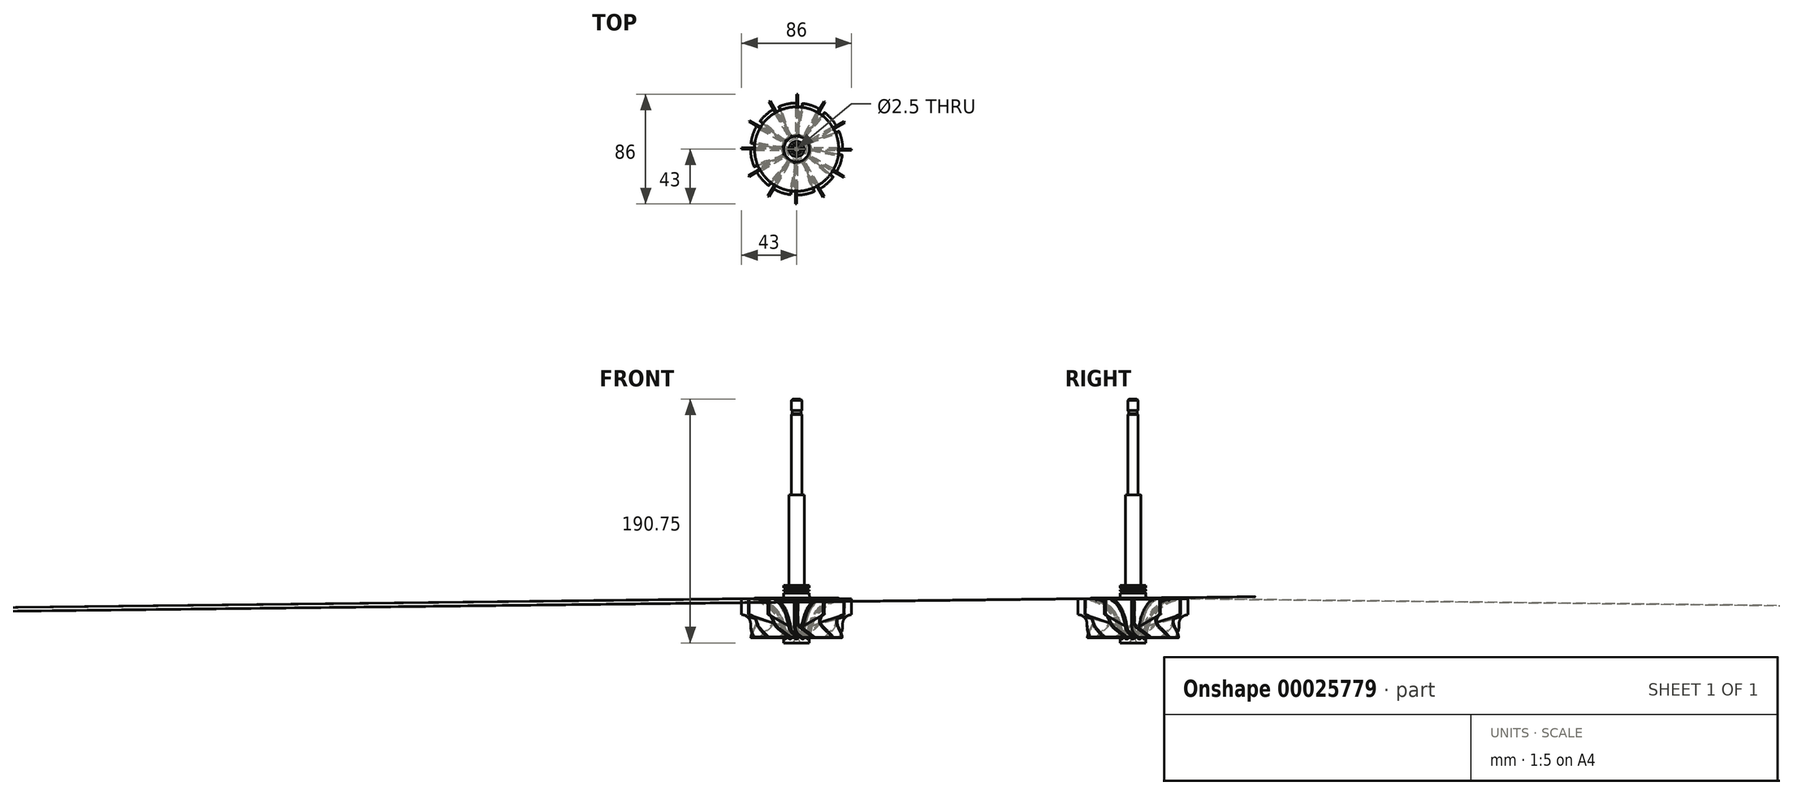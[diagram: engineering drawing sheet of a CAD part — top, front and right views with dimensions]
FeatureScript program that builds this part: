
annotation { "Feature Type Name" : "Feature", "Feature Type Description" : "" }
export const myFeature = defineFeature(function(context is Context, id is Id, definition is map)
    precondition{}
    {
        {
            var Q0;
            Q0=qCreatedBy(makeId("Front.planeOp"),FACE);
            var sketch = newSketch(context, id + "F0", { "sketchPlane" : qUnion([Q0])});
            skLineSegment(sketch, "E0", {"start": v(-6, -75) * mm, "end": v(-6, -145.75) * mm});
            skLineSegment(sketch, "E1", {"start": v(-43, -155.75) * mm, "end": v(-43, -168.75) * mm, "construction": true});
            skLineSegment(sketch, "E2", {"start": v(-43, -155.75) * mm, "end": v(-32.5, -155.75) * mm, "construction": true});
            skLineSegment(sketch, "E3", {"start": v(-10, -145.75) * mm, "end": v(-6, -145.75) * mm});
            skLineSegment(sketch, "E4", {"start": v(-6, -75) * mm, "end": v(-4, -75) * mm});
            skLineSegment(sketch, "E5", {"start": v(-4, 0) * mm, "end": v(0, 0) * mm});
            skLineSegment(sketch, "E6", {"start": v(0, 0) * mm, "end": v(0, -190.75) * mm});
            skLineSegment(sketch, "E7", {"start": v(-4, 0) * mm, "end": v(-4, -9) * mm});
            skLineSegment(sketch, "E8", {"start": v(-3.4, -9) * mm, "end": v(-3.4, -11.4) * mm});
            skLineSegment(sketch, "E9", {"start": v(-3.4, -11.4) * mm, "end": v(-4, -12) * mm});
            skLineSegment(sketch, "E10", {"start": v(-4, -12) * mm, "end": v(-4, -75) * mm});
            skLineSegment(sketch, "E11", {"start": v(-4, -9) * mm, "end": v(-3.4, -9) * mm});
            skLineSegment(sketch, "E12", {"start": v(-10, -145.75) * mm, "end": v(-10, -147.75) * mm});
            skLineSegment(sketch, "E13", {"start": v(-36, -175.75) * mm, "end": v(-36, -186.75) * mm, "construction": true});
            skLineSegment(sketch, "E14", {"start": v(-43, -168.75) * mm, "end": v(-43, -168.75) * mm});
            skLineSegment(sketch, "E15", {"start": v(-36, -186.75) * mm, "end": v(-10, -186.75) * mm, "construction": true});
            skLineSegment(sketch, "E16", {"start": v(-10, -186.75) * mm, "end": v(-10, -190.75) * mm});
            skLineSegment(sketch, "E17", {"start": v(-10, -190.75) * mm, "end": v(0, -190.75) * mm});
            skPoint(sketch, "E18.visualSharp", {"position": v(-36, -168.75) * mm});
            skArc(sketch, "E18.filletArc", {"start": v(-36, -175.75) * mm, "mid": v(-38.05, -170.8) * mm, "end": v(-43, -168.75) * mm, "construction": true});
            skLineSegment(sketch, "E19", {"start": v(-32.5, -155.75) * mm, "end": v(-32.5, -156.75) * mm, "construction": true});
            skArc(sketch, "E20", {"start": v(-32.5, -155.75) * mm, "mid": v(-33, -156.25) * mm, "end": v(-32.5, -156.75) * mm});
            skArc(sketch, "E21", {"start": v(-10, -186.75) * mm, "mid": v(-16.25, -168) * mm, "end": v(-32.5, -156.75) * mm});
            skLineSegment(sketch, "E22", {"start": v(-32.5, -155.75) * mm, "end": v(-10, -155.75) * mm});
            skLineSegment(sketch, "E23", {"start": v(-2.9, -190.75) * mm, "end": v(-1.5, -188.32) * mm});
            skLineSegment(sketch, "E24", {"start": v(-1.5, -188.32) * mm, "end": v(-1.5, -186.8) * mm});
            skLineSegment(sketch, "E25", {"start": v(-1.5, -186.8) * mm, "end": v(0, -185.9) * mm});
            skLineSegment(sketch, "E26", {"start": v(-8, -147.75) * mm, "end": v(-8, -149.25) * mm});
            skLineSegment(sketch, "E27", {"start": v(-8, -147.75) * mm, "end": v(-10, -147.75) * mm});
            skLineSegment(sketch, "E28", {"start": v(-8, -149.25) * mm, "end": v(-10, -149.25) * mm});
            skLineSegment(sketch, "E29", {"start": v(-8, -150.25) * mm, "end": v(-10, -150.25) * mm});
            skLineSegment(sketch, "E30", {"start": v(-8, -151.75) * mm, "end": v(-10, -151.75) * mm});
            skPoint(sketch, "E31.orphan", {"position": v(-8, -155.75) * mm});
            skLineSegment(sketch, "E32.trimOffspring", {"start": v(-8, -150.25) * mm, "end": v(-8, -151.75) * mm});
            skLineSegment(sketch, "E33.trimOffspring", {"start": v(-10, -149.25) * mm, "end": v(-10, -150.25) * mm});
            skLineSegment(sketch, "E34.trimOffspring", {"start": v(-10, -151.75) * mm, "end": v(-10, -155.75) * mm});
            skSolve(sketch);
        }
        {
            var Q0;
            Q0 = qSketchRegion(id + "F0", true);
            var Q1;
            Q1=sQuery(id+"F0.wireOp",EDGE,"E6");
            revolve(context, id + "F1", {"entities" : qUnion([Q0]), "axis" : qUnion([Q1]), "revolveType" : RevolveType.FULL});
        }
        {
            var Q0;
            Q0=makeQuery(id+"F1.opRevolve","SWEPT_EDGE",EDGE,{"disambiguationData":[OSD([sQuery(id+"F0.wireOp",EDGE,"E22"),sQuery(id+"F0.wireOp",EDGE,"E34.trimOffspring")])]});
            fillet(context, id + "F2", {"entities" : qUnion([Q0]), "radius" : 2 * mm, "tangentPropagation" : true, "allowEdgeOverflow" : false});
        }
        {
            var Q0;
            Q0=makeQuery(id+"F1.opRevolve","SWEPT_EDGE",EDGE,{"disambiguationData":[OSD([sQuery(id+"F0.wireOp",EDGE,"E5"),sQuery(id+"F0.wireOp",EDGE,"E7")])]});
            chamfer(context, id + "F3", {"entities" : qUnion([Q0]), "width" : 1 * mm, "tangentPropagation" : true});
        }
        {
            var Q0;
            Q0=qCreatedBy(makeId("Front.planeOp"),FACE);
            var sketch = newSketch(context, id + "F4", { "sketchPlane" : qUnion([Q0])});
            skLineSegment(sketch, "E35", {"start": v(0, -1.47) * mm, "end": v(0, -247.78) * mm, "construction": true});
            skLineSegment(sketch, "E36", {"start": v(0, -155.75) * mm, "end": v(0, -181.26) * mm});
            skPoint(sketch, "E37.orphan", {"position": v(0.08, -187.45) * mm});
            skLineSegment(sketch, "E38", {"start": v(3, -186.75) * mm, "end": v(1.76, -185.5) * mm});
            skPoint(sketch, "E39.visualSharp", {"position": v(0, -183.75) * mm});
            skArc(sketch, "E39.filletArc", {"start": v(0, -181.26) * mm, "mid": v(0.46, -183.56) * mm, "end": v(1.76, -185.5) * mm});
            skLineSegment(sketch, "E40.0", {"start": v(1.59, -186.75) * mm, "end": v(1.05, -186.21) * mm});
            skArc(sketch, "E40.1", {"start": v(-1, -181.26) * mm, "mid": v(-0.47, -183.94) * mm, "end": v(1.05, -186.21) * mm});
            skLineSegment(sketch, "E40.2", {"start": v(-1, -155.75) * mm, "end": v(-1, -181.26) * mm});
            skLineSegment(sketch, "E41", {"start": v(-1, -155.75) * mm, "end": v(0, -155.75) * mm});
            skLineSegment(sketch, "E42", {"start": v(3, -186.75) * mm, "end": v(1.59, -186.75) * mm});
            skSolve(sketch);
        }
        {
            var Q0;
            Q0=qCreatedBy(makeId("Front.planeOp"),FACE);
            cPlane(context, id + "F5", {"entities" : qUnion([Q0]), "cplaneType" : CPlaneType.OFFSET, "offset" : 43 * mm, "width" : 150 * mm, "height" : 150 * mm});
        }
        {
            var Q0;
            Q0=qCreatedBy(id+"F5.planeOp",FACE);
            var sketch = newSketch(context, id + "F6", { "sketchPlane" : qUnion([Q0])});
            skLineSegment(sketch, "E43", {"start": v(0, -186.75) * mm, "end": v(18, -186.75) * mm, "construction": true});
            skLineSegment(sketch, "E44", {"start": v(0, -156.25) * mm, "end": v(0, -168.75) * mm});
            skLineSegment(sketch, "E45", {"start": v(18, -186.75) * mm, "end": v(4.42, -177.24) * mm});
            skArc(sketch, "E46", {"start": v(0, -168.75) * mm, "mid": v(1.17, -173.54) * mm, "end": v(4.42, -177.24) * mm});
            skLineSegment(sketch, "E47.0", {"start": v(16.26, -186.75) * mm, "end": v(3.85, -178.06) * mm});
            skArc(sketch, "E47.1", {"start": v(-1, -168.75) * mm, "mid": v(0.28, -174) * mm, "end": v(3.85, -178.06) * mm});
            skLineSegment(sketch, "E47.2", {"start": v(-1, -156.25) * mm, "end": v(-1, -168.75) * mm});
            skLineSegment(sketch, "E48", {"start": v(18, -186.75) * mm, "end": v(16.26, -186.75) * mm});
            skPoint(sketch, "E49.orphan", {"position": v(-14.5, -155.75) * mm});
            skPoint(sketch, "E50.orphan", {"position": v(14.5, -155.75) * mm});
            skLineSegment(sketch, "E51", {"start": v(0, -156.25) * mm, "end": v(-1, -156.25) * mm});
            skPoint(sketch, "E52.orphan", {"position": v(0, -155.75) * mm});
            skSolve(sketch);
        }
        {
            var Q1;
            Q1 = qSketchRegion(id + "F4", true);
            var Q2;
            Q2 = qSketchRegion(id + "F6", true);
            loft(context, id + "F7", {"operationType" : NewBodyOperationType.ADD, "sheetProfilesArray" : [{ "sheetProfileEntities" : qUnion([Q1]) }, { "sheetProfileEntities" : qUnion([Q2]) }]});
        }
        {
            var Q0;
            Q0=makeQuery(id+"F7.opLoft","SWEPT_FACE",FACE,{"disambiguationData":[OSD([sQuery(id+"F4.wireOp",EDGE,"E40.0"),sQuery(id+"F4.wireOp",EDGE,"E40.1"),sQuery(id+"F4.wireOp",EDGE,"E40.2"),sQuery(id+"F6.wireOp",EDGE,"E47.0"),sQuery(id+"F6.wireOp",EDGE,"E47.1"),sQuery(id+"F6.wireOp",EDGE,"E47.2")])]});
            var Q1;
            Q1=makeQuery(id+"F7.opLoft","SWEPT_FACE",FACE,{"disambiguationData":[OSD([sQuery(id+"F4.wireOp",EDGE,"E38"),sQuery(id+"F4.wireOp",EDGE,"E40.0"),sQuery(id+"F4.wireOp",EDGE,"E42"),sQuery(id+"F6.wireOp",EDGE,"E45"),sQuery(id+"F6.wireOp",EDGE,"E47.0"),sQuery(id+"F6.wireOp",EDGE,"E48")])]});
            var Q2;
            Q2=makeQuery(id+"F7.opLoft","CAP_FACE",FACE,{"disambiguationData":[OSD([makeQuery(id+"F6.imprint","IMPRINT",FACE,{"disambiguationData":[TD([[makeQuery(id+"F6.imprint","IMPRINT",EDGE,{"derivedFrom":sQuery(id+"F6.wireOp",EDGE,"E44")}),-1.0]])]})])],"isStart":true});
            var Q3;
            Q3=makeQuery(id+"F7.opLoft","SWEPT_FACE",FACE,{"disambiguationData":[OSD([sQuery(id+"F4.wireOp",EDGE,"E38"),sQuery(id+"F4.wireOp",EDGE,"E39.filletArc"),sQuery(id+"F4.wireOp",EDGE,"E42"),sQuery(id+"F6.wireOp",EDGE,"E45"),sQuery(id+"F6.wireOp",EDGE,"E46"),sQuery(id+"F6.wireOp",EDGE,"E48")])]});
            var Q4;
            Q4=makeQuery(id+"F7.opLoft","SWEPT_FACE",FACE,{"disambiguationData":[OSD([sQuery(id+"F4.wireOp",EDGE,"E36"),sQuery(id+"F4.wireOp",EDGE,"E39.filletArc"),sQuery(id+"F4.wireOp",EDGE,"E41"),sQuery(id+"F6.wireOp",EDGE,"E44"),sQuery(id+"F6.wireOp",EDGE,"E46"),sQuery(id+"F6.wireOp",EDGE,"E51")])]});
            var Q5;
            Q5=makeQuery(id+"F7.opLoft","SWEPT_FACE",FACE,{"disambiguationData":[OSD([sQuery(id+"F4.wireOp",EDGE,"E40.1"),sQuery(id+"F4.wireOp",EDGE,"E40.2"),sQuery(id+"F4.wireOp",EDGE,"E41"),sQuery(id+"F6.wireOp",EDGE,"E47.1"),sQuery(id+"F6.wireOp",EDGE,"E47.2"),sQuery(id+"F6.wireOp",EDGE,"E51")])]});
            var Q6;
            Q6=makeQuery(id+"F7.opLoft","SWEPT_FACE",FACE,{"disambiguationData":[OSD([sQuery(id+"F4.wireOp",EDGE,"E36"),sQuery(id+"F4.wireOp",EDGE,"E40.2"),sQuery(id+"F4.wireOp",EDGE,"E41"),sQuery(id+"F6.wireOp",EDGE,"E44"),sQuery(id+"F6.wireOp",EDGE,"E47.2"),sQuery(id+"F6.wireOp",EDGE,"E51")])]});
            var Q7;
            Q7=makeQuery(id+"F1.opRevolve","SWEPT_FACE",FACE,{"disambiguationData":[OSD([sQuery(id+"F0.wireOp",EDGE,"E0")])]});
            circularPattern(context, id + "F8", {"faces" : qUnion([Q0, Q1, Q2, Q3, Q4, Q5, Q6]), "axis" : qUnion([Q7]), "angle" : 30 * degree, "instanceCount" : 12, "patternType" : PatternType.FACE});
        }
        {
            var Q0;
            Q0=qCreatedBy(makeId("Front.planeOp"),FACE);
            var sketch = newSketch(context, id + "F9", { "sketchPlane" : qUnion([Q0])});
            skLineSegment(sketch, "E53.0", {"start": v(43, -156.25) * mm, "end": v(43, -168.75) * mm});
            skLineSegment(sketch, "E54", {"start": v(43, -168.75) * mm, "end": v(43, -168.75) * mm});
            skLineSegment(sketch, "E55", {"start": v(36, -175.75) * mm, "end": v(36, -190.75) * mm});
            skLineSegment(sketch, "E56", {"start": v(0, 28.12) * mm, "end": v(0, -228.95) * mm, "construction": true});
            skLineSegment(sketch, "E57", {"start": v(43, -168.75) * mm, "end": v(50.1, -168.75) * mm});
            skLineSegment(sketch, "E58.0", {"start": v(-10, -190.75) * mm, "end": v(10, -190.75) * mm});
            skLineSegment(sketch, "E59", {"start": v(36, -190.75) * mm, "end": v(50.1, -190.75) * mm});
            skLineSegment(sketch, "E60", {"start": v(50.1, -168.75) * mm, "end": v(50.1, -190.75) * mm});
            skPoint(sketch, "E61.visualSharp", {"position": v(36, -168.75) * mm});
            skArc(sketch, "E61.filletArc", {"start": v(43, -168.75) * mm, "mid": v(38.05, -170.8) * mm, "end": v(36, -175.75) * mm});
            skSolve(sketch);
        }
        {
            var Q0;
            Q0 = qSketchRegion(id + "F9", true);
            var Q1;
            Q1=sQuery(id+"F9.wireOp",EDGE,"E56");
            revolve(context, id + "F10", {"operationType" : NewBodyOperationType.REMOVE, "entities" : qUnion([Q0]), "axis" : qUnion([Q1]), "revolveType" : RevolveType.FULL, "oppositeDirection" : true});
        }
        {
            var Q0;
            Q0=qCreatedBy(makeId("Front.planeOp"),FACE);
            var sketch = newSketch(context, id + "F11", { "sketchPlane" : qUnion([Q0])});
            skLineSegment(sketch, "E62", {"start": v(0, 44.53) * mm, "end": v(0, -214.06) * mm, "construction": true});
            skLineSegment(sketch, "E63.0", {"start": v(0, -190.75) * mm, "end": v(2.98, -190.75) * mm});
            skLineSegment(sketch, "E64", {"start": v(0, -190.75) * mm, "end": v(0, -185) * mm});
            skLineSegment(sketch, "E65", {"start": v(0, -185) * mm, "end": v(1.25, -185.75) * mm});
            skLineSegment(sketch, "E66", {"start": v(1.25, -185.75) * mm, "end": v(1.25, -187.75) * mm});
            skLineSegment(sketch, "E67", {"start": v(1.25, -187.75) * mm, "end": v(2.98, -190.75) * mm});
            skPoint(sketch, "E68.orphan", {"position": v(10, -190.75) * mm});
            skPoint(sketch, "E69.orphan", {"position": v(-10, -190.75) * mm});
            skSolve(sketch);
        }
        {
            var Q0;
            Q0 = qSketchRegion(id + "F11", true);
            var Q1;
            Q1=sQuery(id+"F11.wireOp",EDGE,"E62");
            revolve(context, id + "F12", {"operationType" : NewBodyOperationType.REMOVE, "entities" : qUnion([Q0]), "axis" : qUnion([Q1]), "revolveType" : RevolveType.FULL, "oppositeDirection" : true});
        }
        {
            var Q0;
            Q0=makeQuery(id+"F8.opPattern","COPY",EDGE,{"derivedFrom":makeQuery(id+"F7.opLoft","SWEPT_EDGE",EDGE,{"disambiguationData":[OSD([sQuery(id+"F4.wireOp",EDGE,"E38"),sQuery(id+"F4.wireOp",EDGE,"E42"),sQuery(id+"F6.wireOp",EDGE,"E45"),sQuery(id+"F6.wireOp",EDGE,"E48")])]}),"instanceName":"4"});
            var Q1;
            Q1=makeQuery(id+"F8.opPattern","COPY",EDGE,{"derivedFrom":makeQuery(id+"F7.opLoft","SWEPT_EDGE",EDGE,{"disambiguationData":[OSD([sQuery(id+"F4.wireOp",EDGE,"E38"),sQuery(id+"F4.wireOp",EDGE,"E42"),sQuery(id+"F6.wireOp",EDGE,"E45"),sQuery(id+"F6.wireOp",EDGE,"E48")])]}),"instanceName":"3"});
            var Q2;
            Q2=makeQuery(id+"F8.opPattern","COPY",EDGE,{"derivedFrom":makeQuery(id+"F7.opLoft","SWEPT_EDGE",EDGE,{"disambiguationData":[OSD([sQuery(id+"F4.wireOp",EDGE,"E38"),sQuery(id+"F4.wireOp",EDGE,"E42"),sQuery(id+"F6.wireOp",EDGE,"E45"),sQuery(id+"F6.wireOp",EDGE,"E48")])]}),"instanceName":"2"});
            var Q3;
            Q3=makeQuery(id+"F8.opPattern","COPY",EDGE,{"derivedFrom":makeQuery(id+"F7.opLoft","SWEPT_EDGE",EDGE,{"disambiguationData":[OSD([sQuery(id+"F4.wireOp",EDGE,"E38"),sQuery(id+"F4.wireOp",EDGE,"E42"),sQuery(id+"F6.wireOp",EDGE,"E45"),sQuery(id+"F6.wireOp",EDGE,"E48")])]}),"instanceName":"1"});
            var Q4;
            Q4=makeQuery(id+"F7.opLoft","SWEPT_EDGE",EDGE,{"disambiguationData":[OSD([sQuery(id+"F4.wireOp",EDGE,"E38"),sQuery(id+"F4.wireOp",EDGE,"E42"),sQuery(id+"F6.wireOp",EDGE,"E45"),sQuery(id+"F6.wireOp",EDGE,"E48")])]});
            var Q5;
            Q5=makeQuery(id+"F8.opPattern","COPY",EDGE,{"derivedFrom":makeQuery(id+"F7.opLoft","SWEPT_EDGE",EDGE,{"disambiguationData":[OSD([sQuery(id+"F4.wireOp",EDGE,"E38"),sQuery(id+"F4.wireOp",EDGE,"E42"),sQuery(id+"F6.wireOp",EDGE,"E45"),sQuery(id+"F6.wireOp",EDGE,"E48")])]}),"instanceName":"11"});
            var Q6;
            Q6=makeQuery(id+"F8.opPattern","COPY",EDGE,{"derivedFrom":makeQuery(id+"F7.opLoft","SWEPT_EDGE",EDGE,{"disambiguationData":[OSD([sQuery(id+"F4.wireOp",EDGE,"E38"),sQuery(id+"F4.wireOp",EDGE,"E42"),sQuery(id+"F6.wireOp",EDGE,"E45"),sQuery(id+"F6.wireOp",EDGE,"E48")])]}),"instanceName":"10"});
            var Q7;
            Q7=makeQuery(id+"F8.opPattern","COPY",EDGE,{"derivedFrom":makeQuery(id+"F7.opLoft","SWEPT_EDGE",EDGE,{"disambiguationData":[OSD([sQuery(id+"F4.wireOp",EDGE,"E38"),sQuery(id+"F4.wireOp",EDGE,"E42"),sQuery(id+"F6.wireOp",EDGE,"E45"),sQuery(id+"F6.wireOp",EDGE,"E48")])]}),"instanceName":"9"});
            var Q8;
            Q8=makeQuery(id+"F8.opPattern","COPY",EDGE,{"derivedFrom":makeQuery(id+"F7.opLoft","SWEPT_EDGE",EDGE,{"disambiguationData":[OSD([sQuery(id+"F4.wireOp",EDGE,"E38"),sQuery(id+"F4.wireOp",EDGE,"E42"),sQuery(id+"F6.wireOp",EDGE,"E45"),sQuery(id+"F6.wireOp",EDGE,"E48")])]}),"instanceName":"8"});
            var Q9;
            Q9=makeQuery(id+"F8.opPattern","COPY",EDGE,{"derivedFrom":makeQuery(id+"F7.opLoft","SWEPT_EDGE",EDGE,{"disambiguationData":[OSD([sQuery(id+"F4.wireOp",EDGE,"E38"),sQuery(id+"F4.wireOp",EDGE,"E42"),sQuery(id+"F6.wireOp",EDGE,"E45"),sQuery(id+"F6.wireOp",EDGE,"E48")])]}),"instanceName":"7"});
            var Q10;
            Q10=makeQuery(id+"F8.opPattern","COPY",EDGE,{"derivedFrom":makeQuery(id+"F7.opLoft","SWEPT_EDGE",EDGE,{"disambiguationData":[OSD([sQuery(id+"F4.wireOp",EDGE,"E38"),sQuery(id+"F4.wireOp",EDGE,"E42"),sQuery(id+"F6.wireOp",EDGE,"E45"),sQuery(id+"F6.wireOp",EDGE,"E48")])]}),"instanceName":"6"});
            var Q11;
            Q11=makeQuery(id+"F8.opPattern","COPY",EDGE,{"derivedFrom":makeQuery(id+"F7.opLoft","SWEPT_EDGE",EDGE,{"disambiguationData":[OSD([sQuery(id+"F4.wireOp",EDGE,"E38"),sQuery(id+"F4.wireOp",EDGE,"E42"),sQuery(id+"F6.wireOp",EDGE,"E45"),sQuery(id+"F6.wireOp",EDGE,"E48")])]}),"instanceName":"5"});
            fillet(context, id + "F13", {"entities" : qUnion([Q0, Q1, Q2, Q3, Q4, Q5, Q6, Q7, Q8, Q9, Q10, Q11]), "radius" : .3 * mm, "tangentPropagation" : true, "allowEdgeOverflow" : false});
        }
        {
            var Q0;
            Q0=makeQuery(id+"F8.opPattern","COPY",EDGE,{"derivedFrom":makeQuery(id+"F7.opLoft","SWEPT_EDGE",EDGE,{"disambiguationData":[OSD([sQuery(id+"F4.wireOp",EDGE,"E40.0"),sQuery(id+"F4.wireOp",EDGE,"E42"),sQuery(id+"F6.wireOp",EDGE,"E47.0"),sQuery(id+"F6.wireOp",EDGE,"E48")])]}),"instanceName":"5"});
            var Q1;
            Q1=makeQuery(id+"F8.opPattern","COPY",EDGE,{"derivedFrom":makeQuery(id+"F7.opLoft","SWEPT_EDGE",EDGE,{"disambiguationData":[OSD([sQuery(id+"F4.wireOp",EDGE,"E40.0"),sQuery(id+"F4.wireOp",EDGE,"E42"),sQuery(id+"F6.wireOp",EDGE,"E47.0"),sQuery(id+"F6.wireOp",EDGE,"E48")])]}),"instanceName":"4"});
            var Q2;
            Q2=makeQuery(id+"F8.opPattern","COPY",EDGE,{"derivedFrom":makeQuery(id+"F7.opLoft","SWEPT_EDGE",EDGE,{"disambiguationData":[OSD([sQuery(id+"F4.wireOp",EDGE,"E40.0"),sQuery(id+"F4.wireOp",EDGE,"E42"),sQuery(id+"F6.wireOp",EDGE,"E47.0"),sQuery(id+"F6.wireOp",EDGE,"E48")])]}),"instanceName":"3"});
            var Q3;
            Q3=makeQuery(id+"F8.opPattern","COPY",EDGE,{"derivedFrom":makeQuery(id+"F7.opLoft","SWEPT_EDGE",EDGE,{"disambiguationData":[OSD([sQuery(id+"F4.wireOp",EDGE,"E40.0"),sQuery(id+"F4.wireOp",EDGE,"E42"),sQuery(id+"F6.wireOp",EDGE,"E47.0"),sQuery(id+"F6.wireOp",EDGE,"E48")])]}),"instanceName":"2"});
            var Q4;
            Q4=makeQuery(id+"F8.opPattern","COPY",EDGE,{"derivedFrom":makeQuery(id+"F7.opLoft","SWEPT_EDGE",EDGE,{"disambiguationData":[OSD([sQuery(id+"F4.wireOp",EDGE,"E40.0"),sQuery(id+"F4.wireOp",EDGE,"E42"),sQuery(id+"F6.wireOp",EDGE,"E47.0"),sQuery(id+"F6.wireOp",EDGE,"E48")])]}),"instanceName":"1"});
            var Q5;
            Q5=makeQuery(id+"F7.opLoft","SWEPT_EDGE",EDGE,{"disambiguationData":[OSD([sQuery(id+"F4.wireOp",EDGE,"E40.0"),sQuery(id+"F4.wireOp",EDGE,"E42"),sQuery(id+"F6.wireOp",EDGE,"E47.0"),sQuery(id+"F6.wireOp",EDGE,"E48")])]});
            var Q6;
            Q6=makeQuery(id+"F8.opPattern","COPY",EDGE,{"derivedFrom":makeQuery(id+"F7.opLoft","SWEPT_EDGE",EDGE,{"disambiguationData":[OSD([sQuery(id+"F4.wireOp",EDGE,"E40.0"),sQuery(id+"F4.wireOp",EDGE,"E42"),sQuery(id+"F6.wireOp",EDGE,"E47.0"),sQuery(id+"F6.wireOp",EDGE,"E48")])]}),"instanceName":"11"});
            var Q7;
            Q7=makeQuery(id+"F8.opPattern","COPY",EDGE,{"derivedFrom":makeQuery(id+"F7.opLoft","SWEPT_EDGE",EDGE,{"disambiguationData":[OSD([sQuery(id+"F4.wireOp",EDGE,"E40.0"),sQuery(id+"F4.wireOp",EDGE,"E42"),sQuery(id+"F6.wireOp",EDGE,"E47.0"),sQuery(id+"F6.wireOp",EDGE,"E48")])]}),"instanceName":"10"});
            var Q8;
            Q8=makeQuery(id+"F8.opPattern","COPY",EDGE,{"derivedFrom":makeQuery(id+"F7.opLoft","SWEPT_EDGE",EDGE,{"disambiguationData":[OSD([sQuery(id+"F4.wireOp",EDGE,"E40.0"),sQuery(id+"F4.wireOp",EDGE,"E42"),sQuery(id+"F6.wireOp",EDGE,"E47.0"),sQuery(id+"F6.wireOp",EDGE,"E48")])]}),"instanceName":"9"});
            var Q9;
            Q9=makeQuery(id+"F8.opPattern","COPY",EDGE,{"derivedFrom":makeQuery(id+"F7.opLoft","SWEPT_EDGE",EDGE,{"disambiguationData":[OSD([sQuery(id+"F4.wireOp",EDGE,"E40.0"),sQuery(id+"F4.wireOp",EDGE,"E42"),sQuery(id+"F6.wireOp",EDGE,"E47.0"),sQuery(id+"F6.wireOp",EDGE,"E48")])]}),"instanceName":"8"});
            var Q10;
            Q10=makeQuery(id+"F8.opPattern","COPY",EDGE,{"derivedFrom":makeQuery(id+"F7.opLoft","SWEPT_EDGE",EDGE,{"disambiguationData":[OSD([sQuery(id+"F4.wireOp",EDGE,"E40.0"),sQuery(id+"F4.wireOp",EDGE,"E42"),sQuery(id+"F6.wireOp",EDGE,"E47.0"),sQuery(id+"F6.wireOp",EDGE,"E48")])]}),"instanceName":"7"});
            var Q11;
            Q11=makeQuery(id+"F8.opPattern","COPY",EDGE,{"derivedFrom":makeQuery(id+"F7.opLoft","SWEPT_EDGE",EDGE,{"disambiguationData":[OSD([sQuery(id+"F4.wireOp",EDGE,"E40.0"),sQuery(id+"F4.wireOp",EDGE,"E42"),sQuery(id+"F6.wireOp",EDGE,"E47.0"),sQuery(id+"F6.wireOp",EDGE,"E48")])]}),"instanceName":"6"});
            fillet(context, id + "F14", {"entities" : qUnion([Q0, Q1, Q2, Q3, Q4, Q5, Q6, Q7, Q8, Q9, Q10, Q11]), "radius" : 1.5 * mm, "tangentPropagation" : true, "allowEdgeOverflow" : false});
        }
        {
            var Q0;
            Q0=makeQuery(id+"F8.opPattern","COPY",EDGE,{"derivedFrom":makeQuery(id+"F7.boolean.opBoolean","INTERSECT",EDGE,{"derivedFrom":[makeQuery(id+"F1.opRevolve","SWEPT_FACE",FACE,{"disambiguationData":[OSD([sQuery(id+"F0.wireOp",EDGE,"E21")])]}),makeQuery(id+"F7.opLoft","SWEPT_FACE",FACE,{"disambiguationData":[OSD([sQuery(id+"F4.wireOp",EDGE,"E36"),sQuery(id+"F4.wireOp",EDGE,"E39.filletArc"),sQuery(id+"F4.wireOp",EDGE,"E41"),sQuery(id+"F6.wireOp",EDGE,"E44"),sQuery(id+"F6.wireOp",EDGE,"E46"),sQuery(id+"F6.wireOp",EDGE,"E51")])]})]}),"instanceName":"5"});
            var Q1;
            Q1=makeQuery(id+"F8.opPattern","COPY",EDGE,{"derivedFrom":makeQuery(id+"F7.boolean.opBoolean","INTERSECT",EDGE,{"derivedFrom":[makeQuery(id+"F1.opRevolve","SWEPT_FACE",FACE,{"disambiguationData":[OSD([sQuery(id+"F0.wireOp",EDGE,"E21")])]}),makeQuery(id+"F7.opLoft","SWEPT_FACE",FACE,{"disambiguationData":[OSD([sQuery(id+"F4.wireOp",EDGE,"E38"),sQuery(id+"F4.wireOp",EDGE,"E39.filletArc"),sQuery(id+"F4.wireOp",EDGE,"E42"),sQuery(id+"F6.wireOp",EDGE,"E45"),sQuery(id+"F6.wireOp",EDGE,"E46"),sQuery(id+"F6.wireOp",EDGE,"E48")])]})]}),"instanceName":"5"});
            var Q2;
            Q2=makeQuery(id+"F13.opFillet","BLEND_EDGE",EDGE,{"blendedFrom":[makeQuery(id+"F8.opPattern","COPY",EDGE,{"derivedFrom":makeQuery(id+"F7.opLoft","SWEPT_EDGE",EDGE,{"disambiguationData":[OSD([sQuery(id+"F4.wireOp",EDGE,"E38"),sQuery(id+"F4.wireOp",EDGE,"E42"),sQuery(id+"F6.wireOp",EDGE,"E45"),sQuery(id+"F6.wireOp",EDGE,"E48")])]}),"instanceName":"5"}),makeQuery(id+"F8.opPattern","SPLIT",FACE,{"disambiguationData":[OD(6.0)],"derivedFrom":makeQuery(id+"F1.opRevolve","SWEPT_FACE",FACE,{"disambiguationData":[OSD([sQuery(id+"F0.wireOp",EDGE,"E21")])]})})],"blendedInto":[makeQuery(id+"F8.opPattern","SPLIT",FACE,{"disambiguationData":[OD(6.0)],"derivedFrom":makeQuery(id+"F1.opRevolve","SWEPT_FACE",FACE,{"disambiguationData":[OSD([sQuery(id+"F0.wireOp",EDGE,"E21")])]})})]});
            var Q3;
            Q3=makeQuery(id+"F8.opPattern","COPY",EDGE,{"derivedFrom":makeQuery(id+"F7.boolean.opBoolean","SPLIT",EDGE,{"disambiguationData":[OD(1.0)],"derivedFrom":makeQuery(id+"F1.opRevolve","SWEPT_EDGE",EDGE,{"disambiguationData":[OSD([sQuery(id+"F0.wireOp",EDGE,"E16"),sQuery(id+"F0.wireOp",EDGE,"E21")])]})}),"instanceName":"5"});
            var Q4;
            Q4=makeQuery(id+"F14.opFillet","BLEND_EDGE",EDGE,{"blendedFrom":[makeQuery(id+"F8.opPattern","COPY",EDGE,{"derivedFrom":makeQuery(id+"F7.opLoft","SWEPT_EDGE",EDGE,{"disambiguationData":[OSD([sQuery(id+"F4.wireOp",EDGE,"E40.0"),sQuery(id+"F4.wireOp",EDGE,"E42"),sQuery(id+"F6.wireOp",EDGE,"E47.0"),sQuery(id+"F6.wireOp",EDGE,"E48")])]}),"instanceName":"5"}),makeQuery(id+"F8.opPattern","SPLIT",FACE,{"disambiguationData":[OD(5.0)],"derivedFrom":makeQuery(id+"F1.opRevolve","SWEPT_FACE",FACE,{"disambiguationData":[OSD([sQuery(id+"F0.wireOp",EDGE,"E21")])]})})],"blendedInto":[makeQuery(id+"F8.opPattern","SPLIT",FACE,{"disambiguationData":[OD(5.0)],"derivedFrom":makeQuery(id+"F1.opRevolve","SWEPT_FACE",FACE,{"disambiguationData":[OSD([sQuery(id+"F0.wireOp",EDGE,"E21")])]})})]});
            var Q5;
            Q5=makeQuery(id+"F8.opPattern","COPY",EDGE,{"derivedFrom":makeQuery(id+"F7.boolean.opBoolean","INTERSECT",EDGE,{"derivedFrom":[makeQuery(id+"F1.opRevolve","SWEPT_FACE",FACE,{"disambiguationData":[OSD([sQuery(id+"F0.wireOp",EDGE,"E21")])]}),makeQuery(id+"F7.opLoft","SWEPT_FACE",FACE,{"disambiguationData":[OSD([sQuery(id+"F4.wireOp",EDGE,"E40.0"),sQuery(id+"F4.wireOp",EDGE,"E40.1"),sQuery(id+"F4.wireOp",EDGE,"E40.2"),sQuery(id+"F6.wireOp",EDGE,"E47.0"),sQuery(id+"F6.wireOp",EDGE,"E47.1"),sQuery(id+"F6.wireOp",EDGE,"E47.2")])]})]}),"instanceName":"5"});
            var Q6;
            Q6=makeQuery(id+"F8.opPattern","COPY",EDGE,{"derivedFrom":makeQuery(id+"F7.boolean.opBoolean","INTERSECT",EDGE,{"derivedFrom":[makeQuery(id+"F1.opRevolve","SWEPT_FACE",FACE,{"disambiguationData":[OSD([sQuery(id+"F0.wireOp",EDGE,"E21")])]}),makeQuery(id+"F7.opLoft","SWEPT_FACE",FACE,{"disambiguationData":[OSD([sQuery(id+"F4.wireOp",EDGE,"E40.1"),sQuery(id+"F4.wireOp",EDGE,"E40.2"),sQuery(id+"F4.wireOp",EDGE,"E41"),sQuery(id+"F6.wireOp",EDGE,"E47.1"),sQuery(id+"F6.wireOp",EDGE,"E47.2"),sQuery(id+"F6.wireOp",EDGE,"E51")])]})]}),"instanceName":"5"});
            var Q7;
            Q7=makeQuery(id+"F8.opPattern","COPY",EDGE,{"derivedFrom":makeQuery(id+"F7.boolean.opBoolean","INTERSECT",EDGE,{"derivedFrom":[makeQuery(id+"F1.opRevolve","SWEPT_FACE",FACE,{"disambiguationData":[OSD([sQuery(id+"F0.wireOp",EDGE,"E20")])]}),makeQuery(id+"F7.opLoft","SWEPT_FACE",FACE,{"disambiguationData":[OSD([sQuery(id+"F4.wireOp",EDGE,"E40.1"),sQuery(id+"F4.wireOp",EDGE,"E40.2"),sQuery(id+"F4.wireOp",EDGE,"E41"),sQuery(id+"F6.wireOp",EDGE,"E47.1"),sQuery(id+"F6.wireOp",EDGE,"E47.2"),sQuery(id+"F6.wireOp",EDGE,"E51")])]})]}),"instanceName":"5"});
            var Q8;
            Q8=makeQuery(id+"F8.opPattern","COPY",EDGE,{"derivedFrom":makeQuery(id+"F7.boolean.opBoolean","INTERSECT",EDGE,{"derivedFrom":[makeQuery(id+"F1.opRevolve","SWEPT_FACE",FACE,{"disambiguationData":[OSD([sQuery(id+"F0.wireOp",EDGE,"E20")])]}),makeQuery(id+"F7.opLoft","SWEPT_FACE",FACE,{"disambiguationData":[OSD([sQuery(id+"F4.wireOp",EDGE,"E36"),sQuery(id+"F4.wireOp",EDGE,"E39.filletArc"),sQuery(id+"F4.wireOp",EDGE,"E41"),sQuery(id+"F6.wireOp",EDGE,"E44"),sQuery(id+"F6.wireOp",EDGE,"E46"),sQuery(id+"F6.wireOp",EDGE,"E51")])]})]}),"instanceName":"5"});
            var Q9;
            Q9=makeQuery(id+"F8.opPattern","COPY",EDGE,{"derivedFrom":makeQuery(id+"F7.boolean.opBoolean","INTERSECT",EDGE,{"derivedFrom":[makeQuery(id+"F1.opRevolve","SWEPT_FACE",FACE,{"disambiguationData":[OSD([sQuery(id+"F0.wireOp",EDGE,"E20")])]}),makeQuery(id+"F7.opLoft","SWEPT_FACE",FACE,{"disambiguationData":[OSD([sQuery(id+"F4.wireOp",EDGE,"E36"),sQuery(id+"F4.wireOp",EDGE,"E40.2"),sQuery(id+"F4.wireOp",EDGE,"E41"),sQuery(id+"F6.wireOp",EDGE,"E44"),sQuery(id+"F6.wireOp",EDGE,"E47.2"),sQuery(id+"F6.wireOp",EDGE,"E51")])]})]}),"instanceName":"5"});
            var Q10;
            Q10=makeQuery(id+"F8.opPattern","COPY",EDGE,{"derivedFrom":makeQuery(id+"F7.boolean.opBoolean","INTERSECT",EDGE,{"derivedFrom":[makeQuery(id+"F1.opRevolve","SWEPT_FACE",FACE,{"disambiguationData":[OSD([sQuery(id+"F0.wireOp",EDGE,"E21")])]}),makeQuery(id+"F7.opLoft","SWEPT_FACE",FACE,{"disambiguationData":[OSD([sQuery(id+"F4.wireOp",EDGE,"E36"),sQuery(id+"F4.wireOp",EDGE,"E39.filletArc"),sQuery(id+"F4.wireOp",EDGE,"E41"),sQuery(id+"F6.wireOp",EDGE,"E44"),sQuery(id+"F6.wireOp",EDGE,"E46"),sQuery(id+"F6.wireOp",EDGE,"E51")])]})]}),"instanceName":"6"});
            var Q11;
            Q11=makeQuery(id+"F8.opPattern","COPY",EDGE,{"derivedFrom":makeQuery(id+"F7.boolean.opBoolean","INTERSECT",EDGE,{"derivedFrom":[makeQuery(id+"F1.opRevolve","SWEPT_FACE",FACE,{"disambiguationData":[OSD([sQuery(id+"F0.wireOp",EDGE,"E21")])]}),makeQuery(id+"F7.opLoft","SWEPT_FACE",FACE,{"disambiguationData":[OSD([sQuery(id+"F4.wireOp",EDGE,"E38"),sQuery(id+"F4.wireOp",EDGE,"E39.filletArc"),sQuery(id+"F4.wireOp",EDGE,"E42"),sQuery(id+"F6.wireOp",EDGE,"E45"),sQuery(id+"F6.wireOp",EDGE,"E46"),sQuery(id+"F6.wireOp",EDGE,"E48")])]})]}),"instanceName":"6"});
            var Q12;
            Q12=makeQuery(id+"F13.opFillet","BLEND_EDGE",EDGE,{"blendedFrom":[makeQuery(id+"F8.opPattern","COPY",EDGE,{"derivedFrom":makeQuery(id+"F7.opLoft","SWEPT_EDGE",EDGE,{"disambiguationData":[OSD([sQuery(id+"F4.wireOp",EDGE,"E38"),sQuery(id+"F4.wireOp",EDGE,"E42"),sQuery(id+"F6.wireOp",EDGE,"E45"),sQuery(id+"F6.wireOp",EDGE,"E48")])]}),"instanceName":"6"}),makeQuery(id+"F8.opPattern","SPLIT",FACE,{"disambiguationData":[OD(7.0)],"derivedFrom":makeQuery(id+"F1.opRevolve","SWEPT_FACE",FACE,{"disambiguationData":[OSD([sQuery(id+"F0.wireOp",EDGE,"E21")])]})})],"blendedInto":[makeQuery(id+"F8.opPattern","SPLIT",FACE,{"disambiguationData":[OD(7.0)],"derivedFrom":makeQuery(id+"F1.opRevolve","SWEPT_FACE",FACE,{"disambiguationData":[OSD([sQuery(id+"F0.wireOp",EDGE,"E21")])]})})]});
            var Q13;
            Q13=makeQuery(id+"F8.opPattern","COPY",EDGE,{"derivedFrom":makeQuery(id+"F7.boolean.opBoolean","SPLIT",EDGE,{"disambiguationData":[OD(1.0)],"derivedFrom":makeQuery(id+"F1.opRevolve","SWEPT_EDGE",EDGE,{"disambiguationData":[OSD([sQuery(id+"F0.wireOp",EDGE,"E16"),sQuery(id+"F0.wireOp",EDGE,"E21")])]})}),"instanceName":"6"});
            var Q14;
            Q14=makeQuery(id+"F14.opFillet","BLEND_EDGE",EDGE,{"blendedFrom":[makeQuery(id+"F8.opPattern","COPY",EDGE,{"derivedFrom":makeQuery(id+"F7.opLoft","SWEPT_EDGE",EDGE,{"disambiguationData":[OSD([sQuery(id+"F4.wireOp",EDGE,"E40.0"),sQuery(id+"F4.wireOp",EDGE,"E42"),sQuery(id+"F6.wireOp",EDGE,"E47.0"),sQuery(id+"F6.wireOp",EDGE,"E48")])]}),"instanceName":"6"}),makeQuery(id+"F8.opPattern","SPLIT",FACE,{"disambiguationData":[OD(6.0)],"derivedFrom":makeQuery(id+"F1.opRevolve","SWEPT_FACE",FACE,{"disambiguationData":[OSD([sQuery(id+"F0.wireOp",EDGE,"E21")])]})})],"blendedInto":[makeQuery(id+"F8.opPattern","SPLIT",FACE,{"disambiguationData":[OD(6.0)],"derivedFrom":makeQuery(id+"F1.opRevolve","SWEPT_FACE",FACE,{"disambiguationData":[OSD([sQuery(id+"F0.wireOp",EDGE,"E21")])]})})]});
            var Q15;
            Q15=makeQuery(id+"F8.opPattern","COPY",EDGE,{"derivedFrom":makeQuery(id+"F7.boolean.opBoolean","INTERSECT",EDGE,{"derivedFrom":[makeQuery(id+"F1.opRevolve","SWEPT_FACE",FACE,{"disambiguationData":[OSD([sQuery(id+"F0.wireOp",EDGE,"E21")])]}),makeQuery(id+"F7.opLoft","SWEPT_FACE",FACE,{"disambiguationData":[OSD([sQuery(id+"F4.wireOp",EDGE,"E40.0"),sQuery(id+"F4.wireOp",EDGE,"E40.1"),sQuery(id+"F4.wireOp",EDGE,"E40.2"),sQuery(id+"F6.wireOp",EDGE,"E47.0"),sQuery(id+"F6.wireOp",EDGE,"E47.1"),sQuery(id+"F6.wireOp",EDGE,"E47.2")])]})]}),"instanceName":"6"});
            var Q16;
            Q16=makeQuery(id+"F8.opPattern","COPY",EDGE,{"derivedFrom":makeQuery(id+"F7.boolean.opBoolean","INTERSECT",EDGE,{"derivedFrom":[makeQuery(id+"F1.opRevolve","SWEPT_FACE",FACE,{"disambiguationData":[OSD([sQuery(id+"F0.wireOp",EDGE,"E21")])]}),makeQuery(id+"F7.opLoft","SWEPT_FACE",FACE,{"disambiguationData":[OSD([sQuery(id+"F4.wireOp",EDGE,"E40.1"),sQuery(id+"F4.wireOp",EDGE,"E40.2"),sQuery(id+"F4.wireOp",EDGE,"E41"),sQuery(id+"F6.wireOp",EDGE,"E47.1"),sQuery(id+"F6.wireOp",EDGE,"E47.2"),sQuery(id+"F6.wireOp",EDGE,"E51")])]})]}),"instanceName":"6"});
            var Q17;
            Q17=makeQuery(id+"F8.opPattern","COPY",EDGE,{"derivedFrom":makeQuery(id+"F7.boolean.opBoolean","INTERSECT",EDGE,{"derivedFrom":[makeQuery(id+"F1.opRevolve","SWEPT_FACE",FACE,{"disambiguationData":[OSD([sQuery(id+"F0.wireOp",EDGE,"E20")])]}),makeQuery(id+"F7.opLoft","SWEPT_FACE",FACE,{"disambiguationData":[OSD([sQuery(id+"F4.wireOp",EDGE,"E40.1"),sQuery(id+"F4.wireOp",EDGE,"E40.2"),sQuery(id+"F4.wireOp",EDGE,"E41"),sQuery(id+"F6.wireOp",EDGE,"E47.1"),sQuery(id+"F6.wireOp",EDGE,"E47.2"),sQuery(id+"F6.wireOp",EDGE,"E51")])]})]}),"instanceName":"6"});
            var Q18;
            Q18=makeQuery(id+"F8.opPattern","COPY",EDGE,{"derivedFrom":makeQuery(id+"F7.boolean.opBoolean","INTERSECT",EDGE,{"derivedFrom":[makeQuery(id+"F1.opRevolve","SWEPT_FACE",FACE,{"disambiguationData":[OSD([sQuery(id+"F0.wireOp",EDGE,"E20")])]}),makeQuery(id+"F7.opLoft","SWEPT_FACE",FACE,{"disambiguationData":[OSD([sQuery(id+"F4.wireOp",EDGE,"E36"),sQuery(id+"F4.wireOp",EDGE,"E39.filletArc"),sQuery(id+"F4.wireOp",EDGE,"E41"),sQuery(id+"F6.wireOp",EDGE,"E44"),sQuery(id+"F6.wireOp",EDGE,"E46"),sQuery(id+"F6.wireOp",EDGE,"E51")])]})]}),"instanceName":"6"});
            var Q19;
            Q19=makeQuery(id+"F8.opPattern","COPY",EDGE,{"derivedFrom":makeQuery(id+"F7.boolean.opBoolean","INTERSECT",EDGE,{"derivedFrom":[makeQuery(id+"F1.opRevolve","SWEPT_FACE",FACE,{"disambiguationData":[OSD([sQuery(id+"F0.wireOp",EDGE,"E20")])]}),makeQuery(id+"F7.opLoft","SWEPT_FACE",FACE,{"disambiguationData":[OSD([sQuery(id+"F4.wireOp",EDGE,"E36"),sQuery(id+"F4.wireOp",EDGE,"E40.2"),sQuery(id+"F4.wireOp",EDGE,"E41"),sQuery(id+"F6.wireOp",EDGE,"E44"),sQuery(id+"F6.wireOp",EDGE,"E47.2"),sQuery(id+"F6.wireOp",EDGE,"E51")])]})]}),"instanceName":"6"});
            var Q20;
            Q20=makeQuery(id+"F8.opPattern","COPY",EDGE,{"derivedFrom":makeQuery(id+"F7.boolean.opBoolean","INTERSECT",EDGE,{"derivedFrom":[makeQuery(id+"F1.opRevolve","SWEPT_FACE",FACE,{"disambiguationData":[OSD([sQuery(id+"F0.wireOp",EDGE,"E21")])]}),makeQuery(id+"F7.opLoft","SWEPT_FACE",FACE,{"disambiguationData":[OSD([sQuery(id+"F4.wireOp",EDGE,"E36"),sQuery(id+"F4.wireOp",EDGE,"E39.filletArc"),sQuery(id+"F4.wireOp",EDGE,"E41"),sQuery(id+"F6.wireOp",EDGE,"E44"),sQuery(id+"F6.wireOp",EDGE,"E46"),sQuery(id+"F6.wireOp",EDGE,"E51")])]})]}),"instanceName":"7"});
            var Q21;
            Q21=makeQuery(id+"F8.opPattern","COPY",EDGE,{"derivedFrom":makeQuery(id+"F7.boolean.opBoolean","INTERSECT",EDGE,{"derivedFrom":[makeQuery(id+"F1.opRevolve","SWEPT_FACE",FACE,{"disambiguationData":[OSD([sQuery(id+"F0.wireOp",EDGE,"E21")])]}),makeQuery(id+"F7.opLoft","SWEPT_FACE",FACE,{"disambiguationData":[OSD([sQuery(id+"F4.wireOp",EDGE,"E38"),sQuery(id+"F4.wireOp",EDGE,"E39.filletArc"),sQuery(id+"F4.wireOp",EDGE,"E42"),sQuery(id+"F6.wireOp",EDGE,"E45"),sQuery(id+"F6.wireOp",EDGE,"E46"),sQuery(id+"F6.wireOp",EDGE,"E48")])]})]}),"instanceName":"7"});
            var Q22;
            Q22=makeQuery(id+"F13.opFillet","BLEND_EDGE",EDGE,{"blendedFrom":[makeQuery(id+"F8.opPattern","COPY",EDGE,{"derivedFrom":makeQuery(id+"F7.opLoft","SWEPT_EDGE",EDGE,{"disambiguationData":[OSD([sQuery(id+"F4.wireOp",EDGE,"E38"),sQuery(id+"F4.wireOp",EDGE,"E42"),sQuery(id+"F6.wireOp",EDGE,"E45"),sQuery(id+"F6.wireOp",EDGE,"E48")])]}),"instanceName":"7"}),makeQuery(id+"F8.opPattern","SPLIT",FACE,{"disambiguationData":[OD(8.0)],"derivedFrom":makeQuery(id+"F1.opRevolve","SWEPT_FACE",FACE,{"disambiguationData":[OSD([sQuery(id+"F0.wireOp",EDGE,"E21")])]})})],"blendedInto":[makeQuery(id+"F8.opPattern","SPLIT",FACE,{"disambiguationData":[OD(8.0)],"derivedFrom":makeQuery(id+"F1.opRevolve","SWEPT_FACE",FACE,{"disambiguationData":[OSD([sQuery(id+"F0.wireOp",EDGE,"E21")])]})})]});
            var Q23;
            Q23=makeQuery(id+"F8.opPattern","COPY",EDGE,{"derivedFrom":makeQuery(id+"F7.boolean.opBoolean","SPLIT",EDGE,{"disambiguationData":[OD(1.0)],"derivedFrom":makeQuery(id+"F1.opRevolve","SWEPT_EDGE",EDGE,{"disambiguationData":[OSD([sQuery(id+"F0.wireOp",EDGE,"E16"),sQuery(id+"F0.wireOp",EDGE,"E21")])]})}),"instanceName":"7"});
            var Q24;
            Q24=makeQuery(id+"F14.opFillet","BLEND_EDGE",EDGE,{"blendedFrom":[makeQuery(id+"F8.opPattern","COPY",EDGE,{"derivedFrom":makeQuery(id+"F7.opLoft","SWEPT_EDGE",EDGE,{"disambiguationData":[OSD([sQuery(id+"F4.wireOp",EDGE,"E40.0"),sQuery(id+"F4.wireOp",EDGE,"E42"),sQuery(id+"F6.wireOp",EDGE,"E47.0"),sQuery(id+"F6.wireOp",EDGE,"E48")])]}),"instanceName":"7"}),makeQuery(id+"F8.opPattern","SPLIT",FACE,{"disambiguationData":[OD(7.0)],"derivedFrom":makeQuery(id+"F1.opRevolve","SWEPT_FACE",FACE,{"disambiguationData":[OSD([sQuery(id+"F0.wireOp",EDGE,"E21")])]})})],"blendedInto":[makeQuery(id+"F8.opPattern","SPLIT",FACE,{"disambiguationData":[OD(7.0)],"derivedFrom":makeQuery(id+"F1.opRevolve","SWEPT_FACE",FACE,{"disambiguationData":[OSD([sQuery(id+"F0.wireOp",EDGE,"E21")])]})})]});
            var Q25;
            Q25=makeQuery(id+"F8.opPattern","COPY",EDGE,{"derivedFrom":makeQuery(id+"F7.boolean.opBoolean","INTERSECT",EDGE,{"derivedFrom":[makeQuery(id+"F1.opRevolve","SWEPT_FACE",FACE,{"disambiguationData":[OSD([sQuery(id+"F0.wireOp",EDGE,"E21")])]}),makeQuery(id+"F7.opLoft","SWEPT_FACE",FACE,{"disambiguationData":[OSD([sQuery(id+"F4.wireOp",EDGE,"E40.0"),sQuery(id+"F4.wireOp",EDGE,"E40.1"),sQuery(id+"F4.wireOp",EDGE,"E40.2"),sQuery(id+"F6.wireOp",EDGE,"E47.0"),sQuery(id+"F6.wireOp",EDGE,"E47.1"),sQuery(id+"F6.wireOp",EDGE,"E47.2")])]})]}),"instanceName":"7"});
            var Q26;
            Q26=makeQuery(id+"F8.opPattern","COPY",EDGE,{"derivedFrom":makeQuery(id+"F7.boolean.opBoolean","INTERSECT",EDGE,{"derivedFrom":[makeQuery(id+"F1.opRevolve","SWEPT_FACE",FACE,{"disambiguationData":[OSD([sQuery(id+"F0.wireOp",EDGE,"E21")])]}),makeQuery(id+"F7.opLoft","SWEPT_FACE",FACE,{"disambiguationData":[OSD([sQuery(id+"F4.wireOp",EDGE,"E40.1"),sQuery(id+"F4.wireOp",EDGE,"E40.2"),sQuery(id+"F4.wireOp",EDGE,"E41"),sQuery(id+"F6.wireOp",EDGE,"E47.1"),sQuery(id+"F6.wireOp",EDGE,"E47.2"),sQuery(id+"F6.wireOp",EDGE,"E51")])]})]}),"instanceName":"7"});
            var Q27;
            Q27=makeQuery(id+"F8.opPattern","COPY",EDGE,{"derivedFrom":makeQuery(id+"F7.boolean.opBoolean","INTERSECT",EDGE,{"derivedFrom":[makeQuery(id+"F1.opRevolve","SWEPT_FACE",FACE,{"disambiguationData":[OSD([sQuery(id+"F0.wireOp",EDGE,"E20")])]}),makeQuery(id+"F7.opLoft","SWEPT_FACE",FACE,{"disambiguationData":[OSD([sQuery(id+"F4.wireOp",EDGE,"E40.1"),sQuery(id+"F4.wireOp",EDGE,"E40.2"),sQuery(id+"F4.wireOp",EDGE,"E41"),sQuery(id+"F6.wireOp",EDGE,"E47.1"),sQuery(id+"F6.wireOp",EDGE,"E47.2"),sQuery(id+"F6.wireOp",EDGE,"E51")])]})]}),"instanceName":"7"});
            var Q28;
            Q28=makeQuery(id+"F8.opPattern","COPY",EDGE,{"derivedFrom":makeQuery(id+"F7.boolean.opBoolean","INTERSECT",EDGE,{"derivedFrom":[makeQuery(id+"F1.opRevolve","SWEPT_FACE",FACE,{"disambiguationData":[OSD([sQuery(id+"F0.wireOp",EDGE,"E20")])]}),makeQuery(id+"F7.opLoft","SWEPT_FACE",FACE,{"disambiguationData":[OSD([sQuery(id+"F4.wireOp",EDGE,"E36"),sQuery(id+"F4.wireOp",EDGE,"E40.2"),sQuery(id+"F4.wireOp",EDGE,"E41"),sQuery(id+"F6.wireOp",EDGE,"E44"),sQuery(id+"F6.wireOp",EDGE,"E47.2"),sQuery(id+"F6.wireOp",EDGE,"E51")])]})]}),"instanceName":"7"});
            var Q29;
            Q29=makeQuery(id+"F8.opPattern","COPY",EDGE,{"derivedFrom":makeQuery(id+"F7.boolean.opBoolean","INTERSECT",EDGE,{"derivedFrom":[makeQuery(id+"F1.opRevolve","SWEPT_FACE",FACE,{"disambiguationData":[OSD([sQuery(id+"F0.wireOp",EDGE,"E20")])]}),makeQuery(id+"F7.opLoft","SWEPT_FACE",FACE,{"disambiguationData":[OSD([sQuery(id+"F4.wireOp",EDGE,"E36"),sQuery(id+"F4.wireOp",EDGE,"E39.filletArc"),sQuery(id+"F4.wireOp",EDGE,"E41"),sQuery(id+"F6.wireOp",EDGE,"E44"),sQuery(id+"F6.wireOp",EDGE,"E46"),sQuery(id+"F6.wireOp",EDGE,"E51")])]})]}),"instanceName":"7"});
            fillet(context, id + "F15", {"entities" : qUnion([Q0, Q1, Q2, Q3, Q4, Q5, Q6, Q7, Q8, Q9, Q10, Q11, Q12, Q13, Q14, Q15, Q16, Q17, Q18, Q19, Q20, Q21, Q22, Q23, Q24, Q25, Q26, Q27, Q28, Q29]), "radius" : 1 * mm, "tangentPropagation" : true, "allowEdgeOverflow" : false});
        }
        {
            var Q0;
            Q0=makeQuery(id+"F8.opPattern","COPY",EDGE,{"derivedFrom":makeQuery(id+"F7.boolean.opBoolean","INTERSECT",EDGE,{"derivedFrom":[makeQuery(id+"F1.opRevolve","SWEPT_FACE",FACE,{"disambiguationData":[OSD([sQuery(id+"F0.wireOp",EDGE,"E21")])]}),makeQuery(id+"F7.opLoft","SWEPT_FACE",FACE,{"disambiguationData":[OSD([sQuery(id+"F4.wireOp",EDGE,"E36"),sQuery(id+"F4.wireOp",EDGE,"E39.filletArc"),sQuery(id+"F4.wireOp",EDGE,"E41"),sQuery(id+"F6.wireOp",EDGE,"E44"),sQuery(id+"F6.wireOp",EDGE,"E46"),sQuery(id+"F6.wireOp",EDGE,"E51")])]})]}),"instanceName":"8"});
            var Q1;
            Q1=makeQuery(id+"F8.opPattern","COPY",EDGE,{"derivedFrom":makeQuery(id+"F7.boolean.opBoolean","INTERSECT",EDGE,{"derivedFrom":[makeQuery(id+"F1.opRevolve","SWEPT_FACE",FACE,{"disambiguationData":[OSD([sQuery(id+"F0.wireOp",EDGE,"E21")])]}),makeQuery(id+"F7.opLoft","SWEPT_FACE",FACE,{"disambiguationData":[OSD([sQuery(id+"F4.wireOp",EDGE,"E38"),sQuery(id+"F4.wireOp",EDGE,"E39.filletArc"),sQuery(id+"F4.wireOp",EDGE,"E42"),sQuery(id+"F6.wireOp",EDGE,"E45"),sQuery(id+"F6.wireOp",EDGE,"E46"),sQuery(id+"F6.wireOp",EDGE,"E48")])]})]}),"instanceName":"8"});
            var Q2;
            Q2=makeQuery(id+"F13.opFillet","BLEND_EDGE",EDGE,{"blendedFrom":[makeQuery(id+"F8.opPattern","COPY",EDGE,{"derivedFrom":makeQuery(id+"F7.opLoft","SWEPT_EDGE",EDGE,{"disambiguationData":[OSD([sQuery(id+"F4.wireOp",EDGE,"E38"),sQuery(id+"F4.wireOp",EDGE,"E42"),sQuery(id+"F6.wireOp",EDGE,"E45"),sQuery(id+"F6.wireOp",EDGE,"E48")])]}),"instanceName":"8"}),makeQuery(id+"F8.opPattern","SPLIT",FACE,{"disambiguationData":[OD(9.0)],"derivedFrom":makeQuery(id+"F1.opRevolve","SWEPT_FACE",FACE,{"disambiguationData":[OSD([sQuery(id+"F0.wireOp",EDGE,"E21")])]})})],"blendedInto":[makeQuery(id+"F8.opPattern","SPLIT",FACE,{"disambiguationData":[OD(9.0)],"derivedFrom":makeQuery(id+"F1.opRevolve","SWEPT_FACE",FACE,{"disambiguationData":[OSD([sQuery(id+"F0.wireOp",EDGE,"E21")])]})})]});
            var Q3;
            Q3=makeQuery(id+"F8.opPattern","COPY",EDGE,{"derivedFrom":makeQuery(id+"F7.boolean.opBoolean","SPLIT",EDGE,{"disambiguationData":[OD(1.0)],"derivedFrom":makeQuery(id+"F1.opRevolve","SWEPT_EDGE",EDGE,{"disambiguationData":[OSD([sQuery(id+"F0.wireOp",EDGE,"E16"),sQuery(id+"F0.wireOp",EDGE,"E21")])]})}),"instanceName":"8"});
            var Q4;
            Q4=makeQuery(id+"F14.opFillet","BLEND_EDGE",EDGE,{"blendedFrom":[makeQuery(id+"F8.opPattern","COPY",EDGE,{"derivedFrom":makeQuery(id+"F7.opLoft","SWEPT_EDGE",EDGE,{"disambiguationData":[OSD([sQuery(id+"F4.wireOp",EDGE,"E40.0"),sQuery(id+"F4.wireOp",EDGE,"E42"),sQuery(id+"F6.wireOp",EDGE,"E47.0"),sQuery(id+"F6.wireOp",EDGE,"E48")])]}),"instanceName":"8"}),makeQuery(id+"F8.opPattern","SPLIT",FACE,{"disambiguationData":[OD(8.0)],"derivedFrom":makeQuery(id+"F1.opRevolve","SWEPT_FACE",FACE,{"disambiguationData":[OSD([sQuery(id+"F0.wireOp",EDGE,"E21")])]})})],"blendedInto":[makeQuery(id+"F8.opPattern","SPLIT",FACE,{"disambiguationData":[OD(8.0)],"derivedFrom":makeQuery(id+"F1.opRevolve","SWEPT_FACE",FACE,{"disambiguationData":[OSD([sQuery(id+"F0.wireOp",EDGE,"E21")])]})})]});
            var Q5;
            Q5=makeQuery(id+"F8.opPattern","COPY",EDGE,{"derivedFrom":makeQuery(id+"F7.boolean.opBoolean","INTERSECT",EDGE,{"derivedFrom":[makeQuery(id+"F1.opRevolve","SWEPT_FACE",FACE,{"disambiguationData":[OSD([sQuery(id+"F0.wireOp",EDGE,"E21")])]}),makeQuery(id+"F7.opLoft","SWEPT_FACE",FACE,{"disambiguationData":[OSD([sQuery(id+"F4.wireOp",EDGE,"E40.0"),sQuery(id+"F4.wireOp",EDGE,"E40.1"),sQuery(id+"F4.wireOp",EDGE,"E40.2"),sQuery(id+"F6.wireOp",EDGE,"E47.0"),sQuery(id+"F6.wireOp",EDGE,"E47.1"),sQuery(id+"F6.wireOp",EDGE,"E47.2")])]})]}),"instanceName":"8"});
            var Q6;
            Q6=makeQuery(id+"F8.opPattern","COPY",EDGE,{"derivedFrom":makeQuery(id+"F7.boolean.opBoolean","INTERSECT",EDGE,{"derivedFrom":[makeQuery(id+"F1.opRevolve","SWEPT_FACE",FACE,{"disambiguationData":[OSD([sQuery(id+"F0.wireOp",EDGE,"E21")])]}),makeQuery(id+"F7.opLoft","SWEPT_FACE",FACE,{"disambiguationData":[OSD([sQuery(id+"F4.wireOp",EDGE,"E40.1"),sQuery(id+"F4.wireOp",EDGE,"E40.2"),sQuery(id+"F4.wireOp",EDGE,"E41"),sQuery(id+"F6.wireOp",EDGE,"E47.1"),sQuery(id+"F6.wireOp",EDGE,"E47.2"),sQuery(id+"F6.wireOp",EDGE,"E51")])]})]}),"instanceName":"8"});
            var Q7;
            Q7=makeQuery(id+"F8.opPattern","COPY",EDGE,{"derivedFrom":makeQuery(id+"F7.boolean.opBoolean","INTERSECT",EDGE,{"derivedFrom":[makeQuery(id+"F1.opRevolve","SWEPT_FACE",FACE,{"disambiguationData":[OSD([sQuery(id+"F0.wireOp",EDGE,"E20")])]}),makeQuery(id+"F7.opLoft","SWEPT_FACE",FACE,{"disambiguationData":[OSD([sQuery(id+"F4.wireOp",EDGE,"E40.1"),sQuery(id+"F4.wireOp",EDGE,"E40.2"),sQuery(id+"F4.wireOp",EDGE,"E41"),sQuery(id+"F6.wireOp",EDGE,"E47.1"),sQuery(id+"F6.wireOp",EDGE,"E47.2"),sQuery(id+"F6.wireOp",EDGE,"E51")])]})]}),"instanceName":"8"});
            var Q8;
            Q8=makeQuery(id+"F8.opPattern","COPY",EDGE,{"derivedFrom":makeQuery(id+"F7.boolean.opBoolean","INTERSECT",EDGE,{"derivedFrom":[makeQuery(id+"F1.opRevolve","SWEPT_FACE",FACE,{"disambiguationData":[OSD([sQuery(id+"F0.wireOp",EDGE,"E20")])]}),makeQuery(id+"F7.opLoft","SWEPT_FACE",FACE,{"disambiguationData":[OSD([sQuery(id+"F4.wireOp",EDGE,"E36"),sQuery(id+"F4.wireOp",EDGE,"E40.2"),sQuery(id+"F4.wireOp",EDGE,"E41"),sQuery(id+"F6.wireOp",EDGE,"E44"),sQuery(id+"F6.wireOp",EDGE,"E47.2"),sQuery(id+"F6.wireOp",EDGE,"E51")])]})]}),"instanceName":"8"});
            var Q9;
            Q9=makeQuery(id+"F8.opPattern","COPY",EDGE,{"derivedFrom":makeQuery(id+"F7.boolean.opBoolean","INTERSECT",EDGE,{"derivedFrom":[makeQuery(id+"F1.opRevolve","SWEPT_FACE",FACE,{"disambiguationData":[OSD([sQuery(id+"F0.wireOp",EDGE,"E20")])]}),makeQuery(id+"F7.opLoft","SWEPT_FACE",FACE,{"disambiguationData":[OSD([sQuery(id+"F4.wireOp",EDGE,"E36"),sQuery(id+"F4.wireOp",EDGE,"E39.filletArc"),sQuery(id+"F4.wireOp",EDGE,"E41"),sQuery(id+"F6.wireOp",EDGE,"E44"),sQuery(id+"F6.wireOp",EDGE,"E46"),sQuery(id+"F6.wireOp",EDGE,"E51")])]})]}),"instanceName":"8"});
            var Q10;
            Q10=makeQuery(id+"F8.opPattern","COPY",EDGE,{"derivedFrom":makeQuery(id+"F7.boolean.opBoolean","INTERSECT",EDGE,{"derivedFrom":[makeQuery(id+"F1.opRevolve","SWEPT_FACE",FACE,{"disambiguationData":[OSD([sQuery(id+"F0.wireOp",EDGE,"E20")])]}),makeQuery(id+"F7.opLoft","SWEPT_FACE",FACE,{"disambiguationData":[OSD([sQuery(id+"F4.wireOp",EDGE,"E36"),sQuery(id+"F4.wireOp",EDGE,"E39.filletArc"),sQuery(id+"F4.wireOp",EDGE,"E41"),sQuery(id+"F6.wireOp",EDGE,"E44"),sQuery(id+"F6.wireOp",EDGE,"E46"),sQuery(id+"F6.wireOp",EDGE,"E51")])]})]}),"instanceName":"9"});
            var Q11;
            Q11=makeQuery(id+"F8.opPattern","COPY",EDGE,{"derivedFrom":makeQuery(id+"F7.boolean.opBoolean","INTERSECT",EDGE,{"derivedFrom":[makeQuery(id+"F1.opRevolve","SWEPT_FACE",FACE,{"disambiguationData":[OSD([sQuery(id+"F0.wireOp",EDGE,"E21")])]}),makeQuery(id+"F7.opLoft","SWEPT_FACE",FACE,{"disambiguationData":[OSD([sQuery(id+"F4.wireOp",EDGE,"E36"),sQuery(id+"F4.wireOp",EDGE,"E39.filletArc"),sQuery(id+"F4.wireOp",EDGE,"E41"),sQuery(id+"F6.wireOp",EDGE,"E44"),sQuery(id+"F6.wireOp",EDGE,"E46"),sQuery(id+"F6.wireOp",EDGE,"E51")])]})]}),"instanceName":"9"});
            var Q12;
            Q12=makeQuery(id+"F8.opPattern","COPY",EDGE,{"derivedFrom":makeQuery(id+"F7.boolean.opBoolean","INTERSECT",EDGE,{"derivedFrom":[makeQuery(id+"F1.opRevolve","SWEPT_FACE",FACE,{"disambiguationData":[OSD([sQuery(id+"F0.wireOp",EDGE,"E21")])]}),makeQuery(id+"F7.opLoft","SWEPT_FACE",FACE,{"disambiguationData":[OSD([sQuery(id+"F4.wireOp",EDGE,"E38"),sQuery(id+"F4.wireOp",EDGE,"E39.filletArc"),sQuery(id+"F4.wireOp",EDGE,"E42"),sQuery(id+"F6.wireOp",EDGE,"E45"),sQuery(id+"F6.wireOp",EDGE,"E46"),sQuery(id+"F6.wireOp",EDGE,"E48")])]})]}),"instanceName":"9"});
            var Q13;
            Q13=makeQuery(id+"F13.opFillet","BLEND_EDGE",EDGE,{"blendedFrom":[makeQuery(id+"F8.opPattern","COPY",EDGE,{"derivedFrom":makeQuery(id+"F7.opLoft","SWEPT_EDGE",EDGE,{"disambiguationData":[OSD([sQuery(id+"F4.wireOp",EDGE,"E38"),sQuery(id+"F4.wireOp",EDGE,"E42"),sQuery(id+"F6.wireOp",EDGE,"E45"),sQuery(id+"F6.wireOp",EDGE,"E48")])]}),"instanceName":"9"}),makeQuery(id+"F8.opPattern","SPLIT",FACE,{"disambiguationData":[OD(10.0)],"derivedFrom":makeQuery(id+"F1.opRevolve","SWEPT_FACE",FACE,{"disambiguationData":[OSD([sQuery(id+"F0.wireOp",EDGE,"E21")])]})})],"blendedInto":[makeQuery(id+"F8.opPattern","SPLIT",FACE,{"disambiguationData":[OD(10.0)],"derivedFrom":makeQuery(id+"F1.opRevolve","SWEPT_FACE",FACE,{"disambiguationData":[OSD([sQuery(id+"F0.wireOp",EDGE,"E21")])]})})]});
            var Q14;
            Q14=makeQuery(id+"F8.opPattern","COPY",EDGE,{"derivedFrom":makeQuery(id+"F7.boolean.opBoolean","SPLIT",EDGE,{"disambiguationData":[OD(1.0)],"derivedFrom":makeQuery(id+"F1.opRevolve","SWEPT_EDGE",EDGE,{"disambiguationData":[OSD([sQuery(id+"F0.wireOp",EDGE,"E16"),sQuery(id+"F0.wireOp",EDGE,"E21")])]})}),"instanceName":"9"});
            var Q15;
            Q15=makeQuery(id+"F14.opFillet","BLEND_EDGE",EDGE,{"blendedFrom":[makeQuery(id+"F8.opPattern","COPY",EDGE,{"derivedFrom":makeQuery(id+"F7.opLoft","SWEPT_EDGE",EDGE,{"disambiguationData":[OSD([sQuery(id+"F4.wireOp",EDGE,"E40.0"),sQuery(id+"F4.wireOp",EDGE,"E42"),sQuery(id+"F6.wireOp",EDGE,"E47.0"),sQuery(id+"F6.wireOp",EDGE,"E48")])]}),"instanceName":"9"}),makeQuery(id+"F8.opPattern","SPLIT",FACE,{"disambiguationData":[OD(9.0)],"derivedFrom":makeQuery(id+"F1.opRevolve","SWEPT_FACE",FACE,{"disambiguationData":[OSD([sQuery(id+"F0.wireOp",EDGE,"E21")])]})})],"blendedInto":[makeQuery(id+"F8.opPattern","SPLIT",FACE,{"disambiguationData":[OD(9.0)],"derivedFrom":makeQuery(id+"F1.opRevolve","SWEPT_FACE",FACE,{"disambiguationData":[OSD([sQuery(id+"F0.wireOp",EDGE,"E21")])]})})]});
            var Q16;
            Q16=makeQuery(id+"F8.opPattern","COPY",EDGE,{"derivedFrom":makeQuery(id+"F7.boolean.opBoolean","INTERSECT",EDGE,{"derivedFrom":[makeQuery(id+"F1.opRevolve","SWEPT_FACE",FACE,{"disambiguationData":[OSD([sQuery(id+"F0.wireOp",EDGE,"E21")])]}),makeQuery(id+"F7.opLoft","SWEPT_FACE",FACE,{"disambiguationData":[OSD([sQuery(id+"F4.wireOp",EDGE,"E40.0"),sQuery(id+"F4.wireOp",EDGE,"E40.1"),sQuery(id+"F4.wireOp",EDGE,"E40.2"),sQuery(id+"F6.wireOp",EDGE,"E47.0"),sQuery(id+"F6.wireOp",EDGE,"E47.1"),sQuery(id+"F6.wireOp",EDGE,"E47.2")])]})]}),"instanceName":"9"});
            var Q17;
            Q17=makeQuery(id+"F8.opPattern","COPY",EDGE,{"derivedFrom":makeQuery(id+"F7.boolean.opBoolean","INTERSECT",EDGE,{"derivedFrom":[makeQuery(id+"F1.opRevolve","SWEPT_FACE",FACE,{"disambiguationData":[OSD([sQuery(id+"F0.wireOp",EDGE,"E21")])]}),makeQuery(id+"F7.opLoft","SWEPT_FACE",FACE,{"disambiguationData":[OSD([sQuery(id+"F4.wireOp",EDGE,"E40.1"),sQuery(id+"F4.wireOp",EDGE,"E40.2"),sQuery(id+"F4.wireOp",EDGE,"E41"),sQuery(id+"F6.wireOp",EDGE,"E47.1"),sQuery(id+"F6.wireOp",EDGE,"E47.2"),sQuery(id+"F6.wireOp",EDGE,"E51")])]})]}),"instanceName":"9"});
            var Q18;
            Q18=makeQuery(id+"F8.opPattern","COPY",EDGE,{"derivedFrom":makeQuery(id+"F7.boolean.opBoolean","INTERSECT",EDGE,{"derivedFrom":[makeQuery(id+"F1.opRevolve","SWEPT_FACE",FACE,{"disambiguationData":[OSD([sQuery(id+"F0.wireOp",EDGE,"E20")])]}),makeQuery(id+"F7.opLoft","SWEPT_FACE",FACE,{"disambiguationData":[OSD([sQuery(id+"F4.wireOp",EDGE,"E40.1"),sQuery(id+"F4.wireOp",EDGE,"E40.2"),sQuery(id+"F4.wireOp",EDGE,"E41"),sQuery(id+"F6.wireOp",EDGE,"E47.1"),sQuery(id+"F6.wireOp",EDGE,"E47.2"),sQuery(id+"F6.wireOp",EDGE,"E51")])]})]}),"instanceName":"9"});
            var Q19;
            Q19=makeQuery(id+"F8.opPattern","COPY",EDGE,{"derivedFrom":makeQuery(id+"F7.boolean.opBoolean","INTERSECT",EDGE,{"derivedFrom":[makeQuery(id+"F1.opRevolve","SWEPT_FACE",FACE,{"disambiguationData":[OSD([sQuery(id+"F0.wireOp",EDGE,"E20")])]}),makeQuery(id+"F7.opLoft","SWEPT_FACE",FACE,{"disambiguationData":[OSD([sQuery(id+"F4.wireOp",EDGE,"E36"),sQuery(id+"F4.wireOp",EDGE,"E40.2"),sQuery(id+"F4.wireOp",EDGE,"E41"),sQuery(id+"F6.wireOp",EDGE,"E44"),sQuery(id+"F6.wireOp",EDGE,"E47.2"),sQuery(id+"F6.wireOp",EDGE,"E51")])]})]}),"instanceName":"9"});
            var Q20;
            Q20=makeQuery(id+"F8.opPattern","COPY",EDGE,{"derivedFrom":makeQuery(id+"F7.boolean.opBoolean","INTERSECT",EDGE,{"derivedFrom":[makeQuery(id+"F1.opRevolve","SWEPT_FACE",FACE,{"disambiguationData":[OSD([sQuery(id+"F0.wireOp",EDGE,"E21")])]}),makeQuery(id+"F7.opLoft","SWEPT_FACE",FACE,{"disambiguationData":[OSD([sQuery(id+"F4.wireOp",EDGE,"E40.1"),sQuery(id+"F4.wireOp",EDGE,"E40.2"),sQuery(id+"F4.wireOp",EDGE,"E41"),sQuery(id+"F6.wireOp",EDGE,"E47.1"),sQuery(id+"F6.wireOp",EDGE,"E47.2"),sQuery(id+"F6.wireOp",EDGE,"E51")])]})]}),"instanceName":"10"});
            var Q21;
            Q21=makeQuery(id+"F8.opPattern","COPY",EDGE,{"derivedFrom":makeQuery(id+"F7.boolean.opBoolean","INTERSECT",EDGE,{"derivedFrom":[makeQuery(id+"F1.opRevolve","SWEPT_FACE",FACE,{"disambiguationData":[OSD([sQuery(id+"F0.wireOp",EDGE,"E21")])]}),makeQuery(id+"F7.opLoft","SWEPT_FACE",FACE,{"disambiguationData":[OSD([sQuery(id+"F4.wireOp",EDGE,"E40.0"),sQuery(id+"F4.wireOp",EDGE,"E40.1"),sQuery(id+"F4.wireOp",EDGE,"E40.2"),sQuery(id+"F6.wireOp",EDGE,"E47.0"),sQuery(id+"F6.wireOp",EDGE,"E47.1"),sQuery(id+"F6.wireOp",EDGE,"E47.2")])]})]}),"instanceName":"10"});
            var Q22;
            Q22=makeQuery(id+"F14.opFillet","BLEND_EDGE",EDGE,{"blendedFrom":[makeQuery(id+"F8.opPattern","COPY",EDGE,{"derivedFrom":makeQuery(id+"F7.opLoft","SWEPT_EDGE",EDGE,{"disambiguationData":[OSD([sQuery(id+"F4.wireOp",EDGE,"E40.0"),sQuery(id+"F4.wireOp",EDGE,"E42"),sQuery(id+"F6.wireOp",EDGE,"E47.0"),sQuery(id+"F6.wireOp",EDGE,"E48")])]}),"instanceName":"10"}),makeQuery(id+"F8.opPattern","SPLIT",FACE,{"disambiguationData":[OD(10.0)],"derivedFrom":makeQuery(id+"F1.opRevolve","SWEPT_FACE",FACE,{"disambiguationData":[OSD([sQuery(id+"F0.wireOp",EDGE,"E21")])]})})],"blendedInto":[makeQuery(id+"F8.opPattern","SPLIT",FACE,{"disambiguationData":[OD(10.0)],"derivedFrom":makeQuery(id+"F1.opRevolve","SWEPT_FACE",FACE,{"disambiguationData":[OSD([sQuery(id+"F0.wireOp",EDGE,"E21")])]})})]});
            var Q23;
            Q23=makeQuery(id+"F8.opPattern","COPY",EDGE,{"derivedFrom":makeQuery(id+"F7.boolean.opBoolean","SPLIT",EDGE,{"disambiguationData":[OD(1.0)],"derivedFrom":makeQuery(id+"F1.opRevolve","SWEPT_EDGE",EDGE,{"disambiguationData":[OSD([sQuery(id+"F0.wireOp",EDGE,"E16"),sQuery(id+"F0.wireOp",EDGE,"E21")])]})}),"instanceName":"10"});
            var Q24;
            Q24=makeQuery(id+"F13.opFillet","BLEND_EDGE",EDGE,{"blendedFrom":[makeQuery(id+"F8.opPattern","COPY",EDGE,{"derivedFrom":makeQuery(id+"F7.opLoft","SWEPT_EDGE",EDGE,{"disambiguationData":[OSD([sQuery(id+"F4.wireOp",EDGE,"E38"),sQuery(id+"F4.wireOp",EDGE,"E42"),sQuery(id+"F6.wireOp",EDGE,"E45"),sQuery(id+"F6.wireOp",EDGE,"E48")])]}),"instanceName":"10"}),makeQuery(id+"F8.opPattern","SPLIT",FACE,{"disambiguationData":[OD(11.0)],"derivedFrom":makeQuery(id+"F1.opRevolve","SWEPT_FACE",FACE,{"disambiguationData":[OSD([sQuery(id+"F0.wireOp",EDGE,"E21")])]})})],"blendedInto":[makeQuery(id+"F8.opPattern","SPLIT",FACE,{"disambiguationData":[OD(11.0)],"derivedFrom":makeQuery(id+"F1.opRevolve","SWEPT_FACE",FACE,{"disambiguationData":[OSD([sQuery(id+"F0.wireOp",EDGE,"E21")])]})})]});
            var Q25;
            Q25=makeQuery(id+"F8.opPattern","COPY",EDGE,{"derivedFrom":makeQuery(id+"F7.boolean.opBoolean","INTERSECT",EDGE,{"derivedFrom":[makeQuery(id+"F1.opRevolve","SWEPT_FACE",FACE,{"disambiguationData":[OSD([sQuery(id+"F0.wireOp",EDGE,"E21")])]}),makeQuery(id+"F7.opLoft","SWEPT_FACE",FACE,{"disambiguationData":[OSD([sQuery(id+"F4.wireOp",EDGE,"E38"),sQuery(id+"F4.wireOp",EDGE,"E39.filletArc"),sQuery(id+"F4.wireOp",EDGE,"E42"),sQuery(id+"F6.wireOp",EDGE,"E45"),sQuery(id+"F6.wireOp",EDGE,"E46"),sQuery(id+"F6.wireOp",EDGE,"E48")])]})]}),"instanceName":"10"});
            var Q26;
            Q26=makeQuery(id+"F8.opPattern","COPY",EDGE,{"derivedFrom":makeQuery(id+"F7.boolean.opBoolean","INTERSECT",EDGE,{"derivedFrom":[makeQuery(id+"F1.opRevolve","SWEPT_FACE",FACE,{"disambiguationData":[OSD([sQuery(id+"F0.wireOp",EDGE,"E21")])]}),makeQuery(id+"F7.opLoft","SWEPT_FACE",FACE,{"disambiguationData":[OSD([sQuery(id+"F4.wireOp",EDGE,"E36"),sQuery(id+"F4.wireOp",EDGE,"E39.filletArc"),sQuery(id+"F4.wireOp",EDGE,"E41"),sQuery(id+"F6.wireOp",EDGE,"E44"),sQuery(id+"F6.wireOp",EDGE,"E46"),sQuery(id+"F6.wireOp",EDGE,"E51")])]})]}),"instanceName":"10"});
            var Q27;
            Q27=makeQuery(id+"F8.opPattern","COPY",EDGE,{"derivedFrom":makeQuery(id+"F7.boolean.opBoolean","INTERSECT",EDGE,{"derivedFrom":[makeQuery(id+"F1.opRevolve","SWEPT_FACE",FACE,{"disambiguationData":[OSD([sQuery(id+"F0.wireOp",EDGE,"E20")])]}),makeQuery(id+"F7.opLoft","SWEPT_FACE",FACE,{"disambiguationData":[OSD([sQuery(id+"F4.wireOp",EDGE,"E36"),sQuery(id+"F4.wireOp",EDGE,"E39.filletArc"),sQuery(id+"F4.wireOp",EDGE,"E41"),sQuery(id+"F6.wireOp",EDGE,"E44"),sQuery(id+"F6.wireOp",EDGE,"E46"),sQuery(id+"F6.wireOp",EDGE,"E51")])]})]}),"instanceName":"10"});
            var Q28;
            Q28=makeQuery(id+"F8.opPattern","COPY",EDGE,{"derivedFrom":makeQuery(id+"F7.boolean.opBoolean","INTERSECT",EDGE,{"derivedFrom":[makeQuery(id+"F1.opRevolve","SWEPT_FACE",FACE,{"disambiguationData":[OSD([sQuery(id+"F0.wireOp",EDGE,"E20")])]}),makeQuery(id+"F7.opLoft","SWEPT_FACE",FACE,{"disambiguationData":[OSD([sQuery(id+"F4.wireOp",EDGE,"E36"),sQuery(id+"F4.wireOp",EDGE,"E40.2"),sQuery(id+"F4.wireOp",EDGE,"E41"),sQuery(id+"F6.wireOp",EDGE,"E44"),sQuery(id+"F6.wireOp",EDGE,"E47.2"),sQuery(id+"F6.wireOp",EDGE,"E51")])]})]}),"instanceName":"10"});
            var Q29;
            Q29=makeQuery(id+"F8.opPattern","COPY",EDGE,{"derivedFrom":makeQuery(id+"F7.boolean.opBoolean","INTERSECT",EDGE,{"derivedFrom":[makeQuery(id+"F1.opRevolve","SWEPT_FACE",FACE,{"disambiguationData":[OSD([sQuery(id+"F0.wireOp",EDGE,"E20")])]}),makeQuery(id+"F7.opLoft","SWEPT_FACE",FACE,{"disambiguationData":[OSD([sQuery(id+"F4.wireOp",EDGE,"E40.1"),sQuery(id+"F4.wireOp",EDGE,"E40.2"),sQuery(id+"F4.wireOp",EDGE,"E41"),sQuery(id+"F6.wireOp",EDGE,"E47.1"),sQuery(id+"F6.wireOp",EDGE,"E47.2"),sQuery(id+"F6.wireOp",EDGE,"E51")])]})]}),"instanceName":"10"});
            fillet(context, id + "F16", {"entities" : qUnion([Q0, Q1, Q2, Q3, Q4, Q5, Q6, Q7, Q8, Q9, Q10, Q11, Q12, Q13, Q14, Q15, Q16, Q17, Q18, Q19, Q20, Q21, Q22, Q23, Q24, Q25, Q26, Q27, Q28, Q29]), "radius" : 1 * mm, "tangentPropagation" : true, "allowEdgeOverflow" : false});
        }
        {
            var Q0;
            Q0=makeQuery(id+"F8.opPattern","COPY",EDGE,{"derivedFrom":makeQuery(id+"F7.boolean.opBoolean","INTERSECT",EDGE,{"derivedFrom":[makeQuery(id+"F1.opRevolve","SWEPT_FACE",FACE,{"disambiguationData":[OSD([sQuery(id+"F0.wireOp",EDGE,"E20")])]}),makeQuery(id+"F7.opLoft","SWEPT_FACE",FACE,{"disambiguationData":[OSD([sQuery(id+"F4.wireOp",EDGE,"E36"),sQuery(id+"F4.wireOp",EDGE,"E39.filletArc"),sQuery(id+"F4.wireOp",EDGE,"E41"),sQuery(id+"F6.wireOp",EDGE,"E44"),sQuery(id+"F6.wireOp",EDGE,"E46"),sQuery(id+"F6.wireOp",EDGE,"E51")])]})]}),"instanceName":"11"});
            var Q1;
            Q1=makeQuery(id+"F8.opPattern","COPY",EDGE,{"derivedFrom":makeQuery(id+"F7.boolean.opBoolean","INTERSECT",EDGE,{"derivedFrom":[makeQuery(id+"F1.opRevolve","SWEPT_FACE",FACE,{"disambiguationData":[OSD([sQuery(id+"F0.wireOp",EDGE,"E21")])]}),makeQuery(id+"F7.opLoft","SWEPT_FACE",FACE,{"disambiguationData":[OSD([sQuery(id+"F4.wireOp",EDGE,"E36"),sQuery(id+"F4.wireOp",EDGE,"E39.filletArc"),sQuery(id+"F4.wireOp",EDGE,"E41"),sQuery(id+"F6.wireOp",EDGE,"E44"),sQuery(id+"F6.wireOp",EDGE,"E46"),sQuery(id+"F6.wireOp",EDGE,"E51")])]})]}),"instanceName":"11"});
            var Q2;
            Q2=makeQuery(id+"F8.opPattern","COPY",EDGE,{"derivedFrom":makeQuery(id+"F7.boolean.opBoolean","INTERSECT",EDGE,{"derivedFrom":[makeQuery(id+"F1.opRevolve","SWEPT_FACE",FACE,{"disambiguationData":[OSD([sQuery(id+"F0.wireOp",EDGE,"E21")])]}),makeQuery(id+"F7.opLoft","SWEPT_FACE",FACE,{"disambiguationData":[OSD([sQuery(id+"F4.wireOp",EDGE,"E38"),sQuery(id+"F4.wireOp",EDGE,"E39.filletArc"),sQuery(id+"F4.wireOp",EDGE,"E42"),sQuery(id+"F6.wireOp",EDGE,"E45"),sQuery(id+"F6.wireOp",EDGE,"E46"),sQuery(id+"F6.wireOp",EDGE,"E48")])]})]}),"instanceName":"11"});
            var Q3;
            Q3=makeQuery(id+"F13.opFillet","BLEND_EDGE",EDGE,{"blendedFrom":[makeQuery(id+"F8.opPattern","COPY",EDGE,{"derivedFrom":makeQuery(id+"F7.opLoft","SWEPT_EDGE",EDGE,{"disambiguationData":[OSD([sQuery(id+"F4.wireOp",EDGE,"E38"),sQuery(id+"F4.wireOp",EDGE,"E42"),sQuery(id+"F6.wireOp",EDGE,"E45"),sQuery(id+"F6.wireOp",EDGE,"E48")])]}),"instanceName":"11"}),makeQuery(id+"F8.opPattern","SPLIT",FACE,{"disambiguationData":[OD(1.0)],"derivedFrom":makeQuery(id+"F1.opRevolve","SWEPT_FACE",FACE,{"disambiguationData":[OSD([sQuery(id+"F0.wireOp",EDGE,"E21")])]})})],"blendedInto":[makeQuery(id+"F8.opPattern","SPLIT",FACE,{"disambiguationData":[OD(1.0)],"derivedFrom":makeQuery(id+"F1.opRevolve","SWEPT_FACE",FACE,{"disambiguationData":[OSD([sQuery(id+"F0.wireOp",EDGE,"E21")])]})})]});
            var Q4;
            Q4=makeQuery(id+"F8.opPattern","COPY",EDGE,{"derivedFrom":makeQuery(id+"F7.boolean.opBoolean","SPLIT",EDGE,{"disambiguationData":[OD(1.0)],"derivedFrom":makeQuery(id+"F1.opRevolve","SWEPT_EDGE",EDGE,{"disambiguationData":[OSD([sQuery(id+"F0.wireOp",EDGE,"E16"),sQuery(id+"F0.wireOp",EDGE,"E21")])]})}),"instanceName":"11"});
            var Q5;
            Q5=makeQuery(id+"F14.opFillet","BLEND_EDGE",EDGE,{"blendedFrom":[makeQuery(id+"F8.opPattern","COPY",EDGE,{"derivedFrom":makeQuery(id+"F7.opLoft","SWEPT_EDGE",EDGE,{"disambiguationData":[OSD([sQuery(id+"F4.wireOp",EDGE,"E40.0"),sQuery(id+"F4.wireOp",EDGE,"E42"),sQuery(id+"F6.wireOp",EDGE,"E47.0"),sQuery(id+"F6.wireOp",EDGE,"E48")])]}),"instanceName":"11"}),makeQuery(id+"F8.opPattern","SPLIT",FACE,{"disambiguationData":[OD(11.0)],"derivedFrom":makeQuery(id+"F1.opRevolve","SWEPT_FACE",FACE,{"disambiguationData":[OSD([sQuery(id+"F0.wireOp",EDGE,"E21")])]})})],"blendedInto":[makeQuery(id+"F8.opPattern","SPLIT",FACE,{"disambiguationData":[OD(11.0)],"derivedFrom":makeQuery(id+"F1.opRevolve","SWEPT_FACE",FACE,{"disambiguationData":[OSD([sQuery(id+"F0.wireOp",EDGE,"E21")])]})})]});
            var Q6;
            Q6=makeQuery(id+"F8.opPattern","COPY",EDGE,{"derivedFrom":makeQuery(id+"F7.boolean.opBoolean","INTERSECT",EDGE,{"derivedFrom":[makeQuery(id+"F1.opRevolve","SWEPT_FACE",FACE,{"disambiguationData":[OSD([sQuery(id+"F0.wireOp",EDGE,"E21")])]}),makeQuery(id+"F7.opLoft","SWEPT_FACE",FACE,{"disambiguationData":[OSD([sQuery(id+"F4.wireOp",EDGE,"E40.0"),sQuery(id+"F4.wireOp",EDGE,"E40.1"),sQuery(id+"F4.wireOp",EDGE,"E40.2"),sQuery(id+"F6.wireOp",EDGE,"E47.0"),sQuery(id+"F6.wireOp",EDGE,"E47.1"),sQuery(id+"F6.wireOp",EDGE,"E47.2")])]})]}),"instanceName":"11"});
            var Q7;
            Q7=makeQuery(id+"F8.opPattern","COPY",EDGE,{"derivedFrom":makeQuery(id+"F7.boolean.opBoolean","INTERSECT",EDGE,{"derivedFrom":[makeQuery(id+"F1.opRevolve","SWEPT_FACE",FACE,{"disambiguationData":[OSD([sQuery(id+"F0.wireOp",EDGE,"E21")])]}),makeQuery(id+"F7.opLoft","SWEPT_FACE",FACE,{"disambiguationData":[OSD([sQuery(id+"F4.wireOp",EDGE,"E40.1"),sQuery(id+"F4.wireOp",EDGE,"E40.2"),sQuery(id+"F4.wireOp",EDGE,"E41"),sQuery(id+"F6.wireOp",EDGE,"E47.1"),sQuery(id+"F6.wireOp",EDGE,"E47.2"),sQuery(id+"F6.wireOp",EDGE,"E51")])]})]}),"instanceName":"11"});
            var Q8;
            Q8=makeQuery(id+"F8.opPattern","COPY",EDGE,{"derivedFrom":makeQuery(id+"F7.boolean.opBoolean","INTERSECT",EDGE,{"derivedFrom":[makeQuery(id+"F1.opRevolve","SWEPT_FACE",FACE,{"disambiguationData":[OSD([sQuery(id+"F0.wireOp",EDGE,"E20")])]}),makeQuery(id+"F7.opLoft","SWEPT_FACE",FACE,{"disambiguationData":[OSD([sQuery(id+"F4.wireOp",EDGE,"E40.1"),sQuery(id+"F4.wireOp",EDGE,"E40.2"),sQuery(id+"F4.wireOp",EDGE,"E41"),sQuery(id+"F6.wireOp",EDGE,"E47.1"),sQuery(id+"F6.wireOp",EDGE,"E47.2"),sQuery(id+"F6.wireOp",EDGE,"E51")])]})]}),"instanceName":"11"});
            var Q9;
            Q9=makeQuery(id+"F8.opPattern","COPY",EDGE,{"derivedFrom":makeQuery(id+"F7.boolean.opBoolean","INTERSECT",EDGE,{"derivedFrom":[makeQuery(id+"F1.opRevolve","SWEPT_FACE",FACE,{"disambiguationData":[OSD([sQuery(id+"F0.wireOp",EDGE,"E20")])]}),makeQuery(id+"F7.opLoft","SWEPT_FACE",FACE,{"disambiguationData":[OSD([sQuery(id+"F4.wireOp",EDGE,"E36"),sQuery(id+"F4.wireOp",EDGE,"E40.2"),sQuery(id+"F4.wireOp",EDGE,"E41"),sQuery(id+"F6.wireOp",EDGE,"E44"),sQuery(id+"F6.wireOp",EDGE,"E47.2"),sQuery(id+"F6.wireOp",EDGE,"E51")])]})]}),"instanceName":"11"});
            var Q10;
            Q10=makeQuery(id+"F7.boolean.opBoolean","INTERSECT",EDGE,{"derivedFrom":[makeQuery(id+"F1.opRevolve","SWEPT_FACE",FACE,{"disambiguationData":[OSD([sQuery(id+"F0.wireOp",EDGE,"E20")])]}),makeQuery(id+"F7.opLoft","SWEPT_FACE",FACE,{"disambiguationData":[OSD([sQuery(id+"F4.wireOp",EDGE,"E36"),sQuery(id+"F4.wireOp",EDGE,"E39.filletArc"),sQuery(id+"F4.wireOp",EDGE,"E41"),sQuery(id+"F6.wireOp",EDGE,"E44"),sQuery(id+"F6.wireOp",EDGE,"E46"),sQuery(id+"F6.wireOp",EDGE,"E51")])]})]});
            var Q11;
            Q11=makeQuery(id+"F7.boolean.opBoolean","INTERSECT",EDGE,{"derivedFrom":[makeQuery(id+"F1.opRevolve","SWEPT_FACE",FACE,{"disambiguationData":[OSD([sQuery(id+"F0.wireOp",EDGE,"E21")])]}),makeQuery(id+"F7.opLoft","SWEPT_FACE",FACE,{"disambiguationData":[OSD([sQuery(id+"F4.wireOp",EDGE,"E36"),sQuery(id+"F4.wireOp",EDGE,"E39.filletArc"),sQuery(id+"F4.wireOp",EDGE,"E41"),sQuery(id+"F6.wireOp",EDGE,"E44"),sQuery(id+"F6.wireOp",EDGE,"E46"),sQuery(id+"F6.wireOp",EDGE,"E51")])]})]});
            var Q12;
            Q12=makeQuery(id+"F7.boolean.opBoolean","INTERSECT",EDGE,{"derivedFrom":[makeQuery(id+"F1.opRevolve","SWEPT_FACE",FACE,{"disambiguationData":[OSD([sQuery(id+"F0.wireOp",EDGE,"E21")])]}),makeQuery(id+"F7.opLoft","SWEPT_FACE",FACE,{"disambiguationData":[OSD([sQuery(id+"F4.wireOp",EDGE,"E38"),sQuery(id+"F4.wireOp",EDGE,"E39.filletArc"),sQuery(id+"F4.wireOp",EDGE,"E42"),sQuery(id+"F6.wireOp",EDGE,"E45"),sQuery(id+"F6.wireOp",EDGE,"E46"),sQuery(id+"F6.wireOp",EDGE,"E48")])]})]});
            var Q13;
            Q13=makeQuery(id+"F13.opFillet","BLEND_EDGE",EDGE,{"blendedFrom":[makeQuery(id+"F7.opLoft","SWEPT_EDGE",EDGE,{"disambiguationData":[OSD([sQuery(id+"F4.wireOp",EDGE,"E38"),sQuery(id+"F4.wireOp",EDGE,"E42"),sQuery(id+"F6.wireOp",EDGE,"E45"),sQuery(id+"F6.wireOp",EDGE,"E48")])]}),makeQuery(id+"F8.opPattern","SPLIT",FACE,{"disambiguationData":[OD(0.0)],"derivedFrom":makeQuery(id+"F1.opRevolve","SWEPT_FACE",FACE,{"disambiguationData":[OSD([sQuery(id+"F0.wireOp",EDGE,"E21")])]})})],"blendedInto":[makeQuery(id+"F8.opPattern","SPLIT",FACE,{"disambiguationData":[OD(0.0)],"derivedFrom":makeQuery(id+"F1.opRevolve","SWEPT_FACE",FACE,{"disambiguationData":[OSD([sQuery(id+"F0.wireOp",EDGE,"E21")])]})})]});
            var Q14;
            Q14=makeQuery(id+"F7.boolean.opBoolean","SPLIT",EDGE,{"disambiguationData":[OD(1.0)],"derivedFrom":makeQuery(id+"F1.opRevolve","SWEPT_EDGE",EDGE,{"disambiguationData":[OSD([sQuery(id+"F0.wireOp",EDGE,"E16"),sQuery(id+"F0.wireOp",EDGE,"E21")])]})});
            var Q15;
            Q15=makeQuery(id+"F14.opFillet","BLEND_EDGE",EDGE,{"blendedFrom":[makeQuery(id+"F7.opLoft","SWEPT_EDGE",EDGE,{"disambiguationData":[OSD([sQuery(id+"F4.wireOp",EDGE,"E40.0"),sQuery(id+"F4.wireOp",EDGE,"E42"),sQuery(id+"F6.wireOp",EDGE,"E47.0"),sQuery(id+"F6.wireOp",EDGE,"E48")])]}),makeQuery(id+"F8.opPattern","SPLIT",FACE,{"disambiguationData":[OD(1.0)],"derivedFrom":makeQuery(id+"F1.opRevolve","SWEPT_FACE",FACE,{"disambiguationData":[OSD([sQuery(id+"F0.wireOp",EDGE,"E21")])]})})],"blendedInto":[makeQuery(id+"F8.opPattern","SPLIT",FACE,{"disambiguationData":[OD(1.0)],"derivedFrom":makeQuery(id+"F1.opRevolve","SWEPT_FACE",FACE,{"disambiguationData":[OSD([sQuery(id+"F0.wireOp",EDGE,"E21")])]})})]});
            var Q16;
            Q16=makeQuery(id+"F7.boolean.opBoolean","INTERSECT",EDGE,{"derivedFrom":[makeQuery(id+"F1.opRevolve","SWEPT_FACE",FACE,{"disambiguationData":[OSD([sQuery(id+"F0.wireOp",EDGE,"E21")])]}),makeQuery(id+"F7.opLoft","SWEPT_FACE",FACE,{"disambiguationData":[OSD([sQuery(id+"F4.wireOp",EDGE,"E40.0"),sQuery(id+"F4.wireOp",EDGE,"E40.1"),sQuery(id+"F4.wireOp",EDGE,"E40.2"),sQuery(id+"F6.wireOp",EDGE,"E47.0"),sQuery(id+"F6.wireOp",EDGE,"E47.1"),sQuery(id+"F6.wireOp",EDGE,"E47.2")])]})]});
            var Q17;
            Q17=makeQuery(id+"F7.boolean.opBoolean","INTERSECT",EDGE,{"derivedFrom":[makeQuery(id+"F1.opRevolve","SWEPT_FACE",FACE,{"disambiguationData":[OSD([sQuery(id+"F0.wireOp",EDGE,"E21")])]}),makeQuery(id+"F7.opLoft","SWEPT_FACE",FACE,{"disambiguationData":[OSD([sQuery(id+"F4.wireOp",EDGE,"E40.1"),sQuery(id+"F4.wireOp",EDGE,"E40.2"),sQuery(id+"F4.wireOp",EDGE,"E41"),sQuery(id+"F6.wireOp",EDGE,"E47.1"),sQuery(id+"F6.wireOp",EDGE,"E47.2"),sQuery(id+"F6.wireOp",EDGE,"E51")])]})]});
            var Q18;
            Q18=makeQuery(id+"F7.boolean.opBoolean","INTERSECT",EDGE,{"derivedFrom":[makeQuery(id+"F1.opRevolve","SWEPT_FACE",FACE,{"disambiguationData":[OSD([sQuery(id+"F0.wireOp",EDGE,"E20")])]}),makeQuery(id+"F7.opLoft","SWEPT_FACE",FACE,{"disambiguationData":[OSD([sQuery(id+"F4.wireOp",EDGE,"E36"),sQuery(id+"F4.wireOp",EDGE,"E40.2"),sQuery(id+"F4.wireOp",EDGE,"E41"),sQuery(id+"F6.wireOp",EDGE,"E44"),sQuery(id+"F6.wireOp",EDGE,"E47.2"),sQuery(id+"F6.wireOp",EDGE,"E51")])]})]});
            var Q19;
            Q19=makeQuery(id+"F7.boolean.opBoolean","INTERSECT",EDGE,{"derivedFrom":[makeQuery(id+"F1.opRevolve","SWEPT_FACE",FACE,{"disambiguationData":[OSD([sQuery(id+"F0.wireOp",EDGE,"E20")])]}),makeQuery(id+"F7.opLoft","SWEPT_FACE",FACE,{"disambiguationData":[OSD([sQuery(id+"F4.wireOp",EDGE,"E40.1"),sQuery(id+"F4.wireOp",EDGE,"E40.2"),sQuery(id+"F4.wireOp",EDGE,"E41"),sQuery(id+"F6.wireOp",EDGE,"E47.1"),sQuery(id+"F6.wireOp",EDGE,"E47.2"),sQuery(id+"F6.wireOp",EDGE,"E51")])]})]});
            var Q20;
            Q20=makeQuery(id+"F8.opPattern","COPY",EDGE,{"derivedFrom":makeQuery(id+"F7.boolean.opBoolean","INTERSECT",EDGE,{"derivedFrom":[makeQuery(id+"F1.opRevolve","SWEPT_FACE",FACE,{"disambiguationData":[OSD([sQuery(id+"F0.wireOp",EDGE,"E20")])]}),makeQuery(id+"F7.opLoft","SWEPT_FACE",FACE,{"disambiguationData":[OSD([sQuery(id+"F4.wireOp",EDGE,"E36"),sQuery(id+"F4.wireOp",EDGE,"E39.filletArc"),sQuery(id+"F4.wireOp",EDGE,"E41"),sQuery(id+"F6.wireOp",EDGE,"E44"),sQuery(id+"F6.wireOp",EDGE,"E46"),sQuery(id+"F6.wireOp",EDGE,"E51")])]})]}),"instanceName":"1"});
            var Q21;
            Q21=makeQuery(id+"F8.opPattern","COPY",EDGE,{"derivedFrom":makeQuery(id+"F7.boolean.opBoolean","INTERSECT",EDGE,{"derivedFrom":[makeQuery(id+"F1.opRevolve","SWEPT_FACE",FACE,{"disambiguationData":[OSD([sQuery(id+"F0.wireOp",EDGE,"E21")])]}),makeQuery(id+"F7.opLoft","SWEPT_FACE",FACE,{"disambiguationData":[OSD([sQuery(id+"F4.wireOp",EDGE,"E36"),sQuery(id+"F4.wireOp",EDGE,"E39.filletArc"),sQuery(id+"F4.wireOp",EDGE,"E41"),sQuery(id+"F6.wireOp",EDGE,"E44"),sQuery(id+"F6.wireOp",EDGE,"E46"),sQuery(id+"F6.wireOp",EDGE,"E51")])]})]}),"instanceName":"1"});
            var Q22;
            Q22=makeQuery(id+"F8.opPattern","COPY",EDGE,{"derivedFrom":makeQuery(id+"F7.boolean.opBoolean","INTERSECT",EDGE,{"derivedFrom":[makeQuery(id+"F1.opRevolve","SWEPT_FACE",FACE,{"disambiguationData":[OSD([sQuery(id+"F0.wireOp",EDGE,"E21")])]}),makeQuery(id+"F7.opLoft","SWEPT_FACE",FACE,{"disambiguationData":[OSD([sQuery(id+"F4.wireOp",EDGE,"E38"),sQuery(id+"F4.wireOp",EDGE,"E39.filletArc"),sQuery(id+"F4.wireOp",EDGE,"E42"),sQuery(id+"F6.wireOp",EDGE,"E45"),sQuery(id+"F6.wireOp",EDGE,"E46"),sQuery(id+"F6.wireOp",EDGE,"E48")])]})]}),"instanceName":"1"});
            var Q23;
            Q23=makeQuery(id+"F13.opFillet","BLEND_EDGE",EDGE,{"blendedFrom":[makeQuery(id+"F8.opPattern","COPY",EDGE,{"derivedFrom":makeQuery(id+"F7.opLoft","SWEPT_EDGE",EDGE,{"disambiguationData":[OSD([sQuery(id+"F4.wireOp",EDGE,"E38"),sQuery(id+"F4.wireOp",EDGE,"E42"),sQuery(id+"F6.wireOp",EDGE,"E45"),sQuery(id+"F6.wireOp",EDGE,"E48")])]}),"instanceName":"1"}),makeQuery(id+"F8.opPattern","SPLIT",FACE,{"disambiguationData":[OD(2.0)],"derivedFrom":makeQuery(id+"F1.opRevolve","SWEPT_FACE",FACE,{"disambiguationData":[OSD([sQuery(id+"F0.wireOp",EDGE,"E21")])]})})],"blendedInto":[makeQuery(id+"F8.opPattern","SPLIT",FACE,{"disambiguationData":[OD(2.0)],"derivedFrom":makeQuery(id+"F1.opRevolve","SWEPT_FACE",FACE,{"disambiguationData":[OSD([sQuery(id+"F0.wireOp",EDGE,"E21")])]})})]});
            var Q24;
            Q24=makeQuery(id+"F8.opPattern","COPY",EDGE,{"derivedFrom":makeQuery(id+"F7.boolean.opBoolean","SPLIT",EDGE,{"disambiguationData":[OD(1.0)],"derivedFrom":makeQuery(id+"F1.opRevolve","SWEPT_EDGE",EDGE,{"disambiguationData":[OSD([sQuery(id+"F0.wireOp",EDGE,"E16"),sQuery(id+"F0.wireOp",EDGE,"E21")])]})}),"instanceName":"1"});
            var Q25;
            Q25=makeQuery(id+"F14.opFillet","BLEND_EDGE",EDGE,{"blendedFrom":[makeQuery(id+"F8.opPattern","COPY",EDGE,{"derivedFrom":makeQuery(id+"F7.opLoft","SWEPT_EDGE",EDGE,{"disambiguationData":[OSD([sQuery(id+"F4.wireOp",EDGE,"E40.0"),sQuery(id+"F4.wireOp",EDGE,"E42"),sQuery(id+"F6.wireOp",EDGE,"E47.0"),sQuery(id+"F6.wireOp",EDGE,"E48")])]}),"instanceName":"1"}),makeQuery(id+"F8.opPattern","SPLIT",FACE,{"disambiguationData":[OD(0.0)],"derivedFrom":makeQuery(id+"F1.opRevolve","SWEPT_FACE",FACE,{"disambiguationData":[OSD([sQuery(id+"F0.wireOp",EDGE,"E21")])]})})],"blendedInto":[makeQuery(id+"F8.opPattern","SPLIT",FACE,{"disambiguationData":[OD(0.0)],"derivedFrom":makeQuery(id+"F1.opRevolve","SWEPT_FACE",FACE,{"disambiguationData":[OSD([sQuery(id+"F0.wireOp",EDGE,"E21")])]})})]});
            var Q26;
            Q26=makeQuery(id+"F8.opPattern","COPY",EDGE,{"derivedFrom":makeQuery(id+"F7.boolean.opBoolean","INTERSECT",EDGE,{"derivedFrom":[makeQuery(id+"F1.opRevolve","SWEPT_FACE",FACE,{"disambiguationData":[OSD([sQuery(id+"F0.wireOp",EDGE,"E21")])]}),makeQuery(id+"F7.opLoft","SWEPT_FACE",FACE,{"disambiguationData":[OSD([sQuery(id+"F4.wireOp",EDGE,"E40.0"),sQuery(id+"F4.wireOp",EDGE,"E40.1"),sQuery(id+"F4.wireOp",EDGE,"E40.2"),sQuery(id+"F6.wireOp",EDGE,"E47.0"),sQuery(id+"F6.wireOp",EDGE,"E47.1"),sQuery(id+"F6.wireOp",EDGE,"E47.2")])]})]}),"instanceName":"1"});
            var Q27;
            Q27=makeQuery(id+"F8.opPattern","COPY",EDGE,{"derivedFrom":makeQuery(id+"F7.boolean.opBoolean","INTERSECT",EDGE,{"derivedFrom":[makeQuery(id+"F1.opRevolve","SWEPT_FACE",FACE,{"disambiguationData":[OSD([sQuery(id+"F0.wireOp",EDGE,"E21")])]}),makeQuery(id+"F7.opLoft","SWEPT_FACE",FACE,{"disambiguationData":[OSD([sQuery(id+"F4.wireOp",EDGE,"E40.1"),sQuery(id+"F4.wireOp",EDGE,"E40.2"),sQuery(id+"F4.wireOp",EDGE,"E41"),sQuery(id+"F6.wireOp",EDGE,"E47.1"),sQuery(id+"F6.wireOp",EDGE,"E47.2"),sQuery(id+"F6.wireOp",EDGE,"E51")])]})]}),"instanceName":"1"});
            var Q28;
            Q28=makeQuery(id+"F8.opPattern","COPY",EDGE,{"derivedFrom":makeQuery(id+"F7.boolean.opBoolean","INTERSECT",EDGE,{"derivedFrom":[makeQuery(id+"F1.opRevolve","SWEPT_FACE",FACE,{"disambiguationData":[OSD([sQuery(id+"F0.wireOp",EDGE,"E20")])]}),makeQuery(id+"F7.opLoft","SWEPT_FACE",FACE,{"disambiguationData":[OSD([sQuery(id+"F4.wireOp",EDGE,"E40.1"),sQuery(id+"F4.wireOp",EDGE,"E40.2"),sQuery(id+"F4.wireOp",EDGE,"E41"),sQuery(id+"F6.wireOp",EDGE,"E47.1"),sQuery(id+"F6.wireOp",EDGE,"E47.2"),sQuery(id+"F6.wireOp",EDGE,"E51")])]})]}),"instanceName":"1"});
            var Q29;
            Q29=makeQuery(id+"F8.opPattern","COPY",EDGE,{"derivedFrom":makeQuery(id+"F7.boolean.opBoolean","INTERSECT",EDGE,{"derivedFrom":[makeQuery(id+"F1.opRevolve","SWEPT_FACE",FACE,{"disambiguationData":[OSD([sQuery(id+"F0.wireOp",EDGE,"E20")])]}),makeQuery(id+"F7.opLoft","SWEPT_FACE",FACE,{"disambiguationData":[OSD([sQuery(id+"F4.wireOp",EDGE,"E36"),sQuery(id+"F4.wireOp",EDGE,"E40.2"),sQuery(id+"F4.wireOp",EDGE,"E41"),sQuery(id+"F6.wireOp",EDGE,"E44"),sQuery(id+"F6.wireOp",EDGE,"E47.2"),sQuery(id+"F6.wireOp",EDGE,"E51")])]})]}),"instanceName":"1"});
            fillet(context, id + "F17", {"entities" : qUnion([Q0, Q1, Q2, Q3, Q4, Q5, Q6, Q7, Q8, Q9, Q10, Q11, Q12, Q13, Q14, Q15, Q16, Q17, Q18, Q19, Q20, Q21, Q22, Q23, Q24, Q25, Q26, Q27, Q28, Q29]), "radius" : 1 * mm, "tangentPropagation" : true, "allowEdgeOverflow" : false});
        }
        {
            var Q0;
            Q0=makeQuery(id+"F8.opPattern","COPY",EDGE,{"derivedFrom":makeQuery(id+"F7.boolean.opBoolean","INTERSECT",EDGE,{"derivedFrom":[makeQuery(id+"F1.opRevolve","SWEPT_FACE",FACE,{"disambiguationData":[OSD([sQuery(id+"F0.wireOp",EDGE,"E20")])]}),makeQuery(id+"F7.opLoft","SWEPT_FACE",FACE,{"disambiguationData":[OSD([sQuery(id+"F4.wireOp",EDGE,"E40.1"),sQuery(id+"F4.wireOp",EDGE,"E40.2"),sQuery(id+"F4.wireOp",EDGE,"E41"),sQuery(id+"F6.wireOp",EDGE,"E47.1"),sQuery(id+"F6.wireOp",EDGE,"E47.2"),sQuery(id+"F6.wireOp",EDGE,"E51")])]})]}),"instanceName":"2"});
            var Q1;
            Q1=makeQuery(id+"F8.opPattern","COPY",EDGE,{"derivedFrom":makeQuery(id+"F7.boolean.opBoolean","INTERSECT",EDGE,{"derivedFrom":[makeQuery(id+"F1.opRevolve","SWEPT_FACE",FACE,{"disambiguationData":[OSD([sQuery(id+"F0.wireOp",EDGE,"E20")])]}),makeQuery(id+"F7.opLoft","SWEPT_FACE",FACE,{"disambiguationData":[OSD([sQuery(id+"F4.wireOp",EDGE,"E36"),sQuery(id+"F4.wireOp",EDGE,"E40.2"),sQuery(id+"F4.wireOp",EDGE,"E41"),sQuery(id+"F6.wireOp",EDGE,"E44"),sQuery(id+"F6.wireOp",EDGE,"E47.2"),sQuery(id+"F6.wireOp",EDGE,"E51")])]})]}),"instanceName":"2"});
            var Q2;
            Q2=makeQuery(id+"F8.opPattern","COPY",EDGE,{"derivedFrom":makeQuery(id+"F7.boolean.opBoolean","INTERSECT",EDGE,{"derivedFrom":[makeQuery(id+"F1.opRevolve","SWEPT_FACE",FACE,{"disambiguationData":[OSD([sQuery(id+"F0.wireOp",EDGE,"E20")])]}),makeQuery(id+"F7.opLoft","SWEPT_FACE",FACE,{"disambiguationData":[OSD([sQuery(id+"F4.wireOp",EDGE,"E36"),sQuery(id+"F4.wireOp",EDGE,"E39.filletArc"),sQuery(id+"F4.wireOp",EDGE,"E41"),sQuery(id+"F6.wireOp",EDGE,"E44"),sQuery(id+"F6.wireOp",EDGE,"E46"),sQuery(id+"F6.wireOp",EDGE,"E51")])]})]}),"instanceName":"2"});
            var Q3;
            Q3=makeQuery(id+"F8.opPattern","COPY",EDGE,{"derivedFrom":makeQuery(id+"F7.boolean.opBoolean","INTERSECT",EDGE,{"derivedFrom":[makeQuery(id+"F1.opRevolve","SWEPT_FACE",FACE,{"disambiguationData":[OSD([sQuery(id+"F0.wireOp",EDGE,"E21")])]}),makeQuery(id+"F7.opLoft","SWEPT_FACE",FACE,{"disambiguationData":[OSD([sQuery(id+"F4.wireOp",EDGE,"E36"),sQuery(id+"F4.wireOp",EDGE,"E39.filletArc"),sQuery(id+"F4.wireOp",EDGE,"E41"),sQuery(id+"F6.wireOp",EDGE,"E44"),sQuery(id+"F6.wireOp",EDGE,"E46"),sQuery(id+"F6.wireOp",EDGE,"E51")])]})]}),"instanceName":"2"});
            var Q4;
            Q4=makeQuery(id+"F8.opPattern","COPY",EDGE,{"derivedFrom":makeQuery(id+"F7.boolean.opBoolean","INTERSECT",EDGE,{"derivedFrom":[makeQuery(id+"F1.opRevolve","SWEPT_FACE",FACE,{"disambiguationData":[OSD([sQuery(id+"F0.wireOp",EDGE,"E20")])]}),makeQuery(id+"F7.opLoft","SWEPT_FACE",FACE,{"disambiguationData":[OSD([sQuery(id+"F4.wireOp",EDGE,"E40.1"),sQuery(id+"F4.wireOp",EDGE,"E40.2"),sQuery(id+"F4.wireOp",EDGE,"E41"),sQuery(id+"F6.wireOp",EDGE,"E47.1"),sQuery(id+"F6.wireOp",EDGE,"E47.2"),sQuery(id+"F6.wireOp",EDGE,"E51")])]})]}),"instanceName":"3"});
            var Q5;
            Q5=makeQuery(id+"F8.opPattern","COPY",EDGE,{"derivedFrom":makeQuery(id+"F7.boolean.opBoolean","INTERSECT",EDGE,{"derivedFrom":[makeQuery(id+"F1.opRevolve","SWEPT_FACE",FACE,{"disambiguationData":[OSD([sQuery(id+"F0.wireOp",EDGE,"E20")])]}),makeQuery(id+"F7.opLoft","SWEPT_FACE",FACE,{"disambiguationData":[OSD([sQuery(id+"F4.wireOp",EDGE,"E36"),sQuery(id+"F4.wireOp",EDGE,"E40.2"),sQuery(id+"F4.wireOp",EDGE,"E41"),sQuery(id+"F6.wireOp",EDGE,"E44"),sQuery(id+"F6.wireOp",EDGE,"E47.2"),sQuery(id+"F6.wireOp",EDGE,"E51")])]})]}),"instanceName":"3"});
            var Q6;
            Q6=makeQuery(id+"F8.opPattern","COPY",EDGE,{"derivedFrom":makeQuery(id+"F7.boolean.opBoolean","INTERSECT",EDGE,{"derivedFrom":[makeQuery(id+"F1.opRevolve","SWEPT_FACE",FACE,{"disambiguationData":[OSD([sQuery(id+"F0.wireOp",EDGE,"E20")])]}),makeQuery(id+"F7.opLoft","SWEPT_FACE",FACE,{"disambiguationData":[OSD([sQuery(id+"F4.wireOp",EDGE,"E36"),sQuery(id+"F4.wireOp",EDGE,"E39.filletArc"),sQuery(id+"F4.wireOp",EDGE,"E41"),sQuery(id+"F6.wireOp",EDGE,"E44"),sQuery(id+"F6.wireOp",EDGE,"E46"),sQuery(id+"F6.wireOp",EDGE,"E51")])]})]}),"instanceName":"3"});
            var Q7;
            Q7=makeQuery(id+"F8.opPattern","COPY",EDGE,{"derivedFrom":makeQuery(id+"F7.boolean.opBoolean","INTERSECT",EDGE,{"derivedFrom":[makeQuery(id+"F1.opRevolve","SWEPT_FACE",FACE,{"disambiguationData":[OSD([sQuery(id+"F0.wireOp",EDGE,"E21")])]}),makeQuery(id+"F7.opLoft","SWEPT_FACE",FACE,{"disambiguationData":[OSD([sQuery(id+"F4.wireOp",EDGE,"E36"),sQuery(id+"F4.wireOp",EDGE,"E39.filletArc"),sQuery(id+"F4.wireOp",EDGE,"E41"),sQuery(id+"F6.wireOp",EDGE,"E44"),sQuery(id+"F6.wireOp",EDGE,"E46"),sQuery(id+"F6.wireOp",EDGE,"E51")])]})]}),"instanceName":"3"});
            var Q8;
            Q8=makeQuery(id+"F8.opPattern","COPY",EDGE,{"derivedFrom":makeQuery(id+"F7.boolean.opBoolean","INTERSECT",EDGE,{"derivedFrom":[makeQuery(id+"F1.opRevolve","SWEPT_FACE",FACE,{"disambiguationData":[OSD([sQuery(id+"F0.wireOp",EDGE,"E20")])]}),makeQuery(id+"F7.opLoft","SWEPT_FACE",FACE,{"disambiguationData":[OSD([sQuery(id+"F4.wireOp",EDGE,"E40.1"),sQuery(id+"F4.wireOp",EDGE,"E40.2"),sQuery(id+"F4.wireOp",EDGE,"E41"),sQuery(id+"F6.wireOp",EDGE,"E47.1"),sQuery(id+"F6.wireOp",EDGE,"E47.2"),sQuery(id+"F6.wireOp",EDGE,"E51")])]})]}),"instanceName":"4"});
            var Q9;
            Q9=makeQuery(id+"F8.opPattern","COPY",EDGE,{"derivedFrom":makeQuery(id+"F7.boolean.opBoolean","INTERSECT",EDGE,{"derivedFrom":[makeQuery(id+"F1.opRevolve","SWEPT_FACE",FACE,{"disambiguationData":[OSD([sQuery(id+"F0.wireOp",EDGE,"E20")])]}),makeQuery(id+"F7.opLoft","SWEPT_FACE",FACE,{"disambiguationData":[OSD([sQuery(id+"F4.wireOp",EDGE,"E36"),sQuery(id+"F4.wireOp",EDGE,"E40.2"),sQuery(id+"F4.wireOp",EDGE,"E41"),sQuery(id+"F6.wireOp",EDGE,"E44"),sQuery(id+"F6.wireOp",EDGE,"E47.2"),sQuery(id+"F6.wireOp",EDGE,"E51")])]})]}),"instanceName":"4"});
            var Q10;
            Q10=makeQuery(id+"F8.opPattern","COPY",EDGE,{"derivedFrom":makeQuery(id+"F7.boolean.opBoolean","INTERSECT",EDGE,{"derivedFrom":[makeQuery(id+"F1.opRevolve","SWEPT_FACE",FACE,{"disambiguationData":[OSD([sQuery(id+"F0.wireOp",EDGE,"E20")])]}),makeQuery(id+"F7.opLoft","SWEPT_FACE",FACE,{"disambiguationData":[OSD([sQuery(id+"F4.wireOp",EDGE,"E36"),sQuery(id+"F4.wireOp",EDGE,"E39.filletArc"),sQuery(id+"F4.wireOp",EDGE,"E41"),sQuery(id+"F6.wireOp",EDGE,"E44"),sQuery(id+"F6.wireOp",EDGE,"E46"),sQuery(id+"F6.wireOp",EDGE,"E51")])]})]}),"instanceName":"4"});
            var Q11;
            Q11=makeQuery(id+"F8.opPattern","COPY",EDGE,{"derivedFrom":makeQuery(id+"F7.boolean.opBoolean","INTERSECT",EDGE,{"derivedFrom":[makeQuery(id+"F1.opRevolve","SWEPT_FACE",FACE,{"disambiguationData":[OSD([sQuery(id+"F0.wireOp",EDGE,"E21")])]}),makeQuery(id+"F7.opLoft","SWEPT_FACE",FACE,{"disambiguationData":[OSD([sQuery(id+"F4.wireOp",EDGE,"E36"),sQuery(id+"F4.wireOp",EDGE,"E39.filletArc"),sQuery(id+"F4.wireOp",EDGE,"E41"),sQuery(id+"F6.wireOp",EDGE,"E44"),sQuery(id+"F6.wireOp",EDGE,"E46"),sQuery(id+"F6.wireOp",EDGE,"E51")])]})]}),"instanceName":"4"});
            fillet(context, id + "F18", {"entities" : qUnion([Q0, Q1, Q2, Q3, Q4, Q5, Q6, Q7, Q8, Q9, Q10, Q11]), "radius" : 1 * mm, "tangentPropagation" : true, "allowEdgeOverflow" : false});
        }
    });
